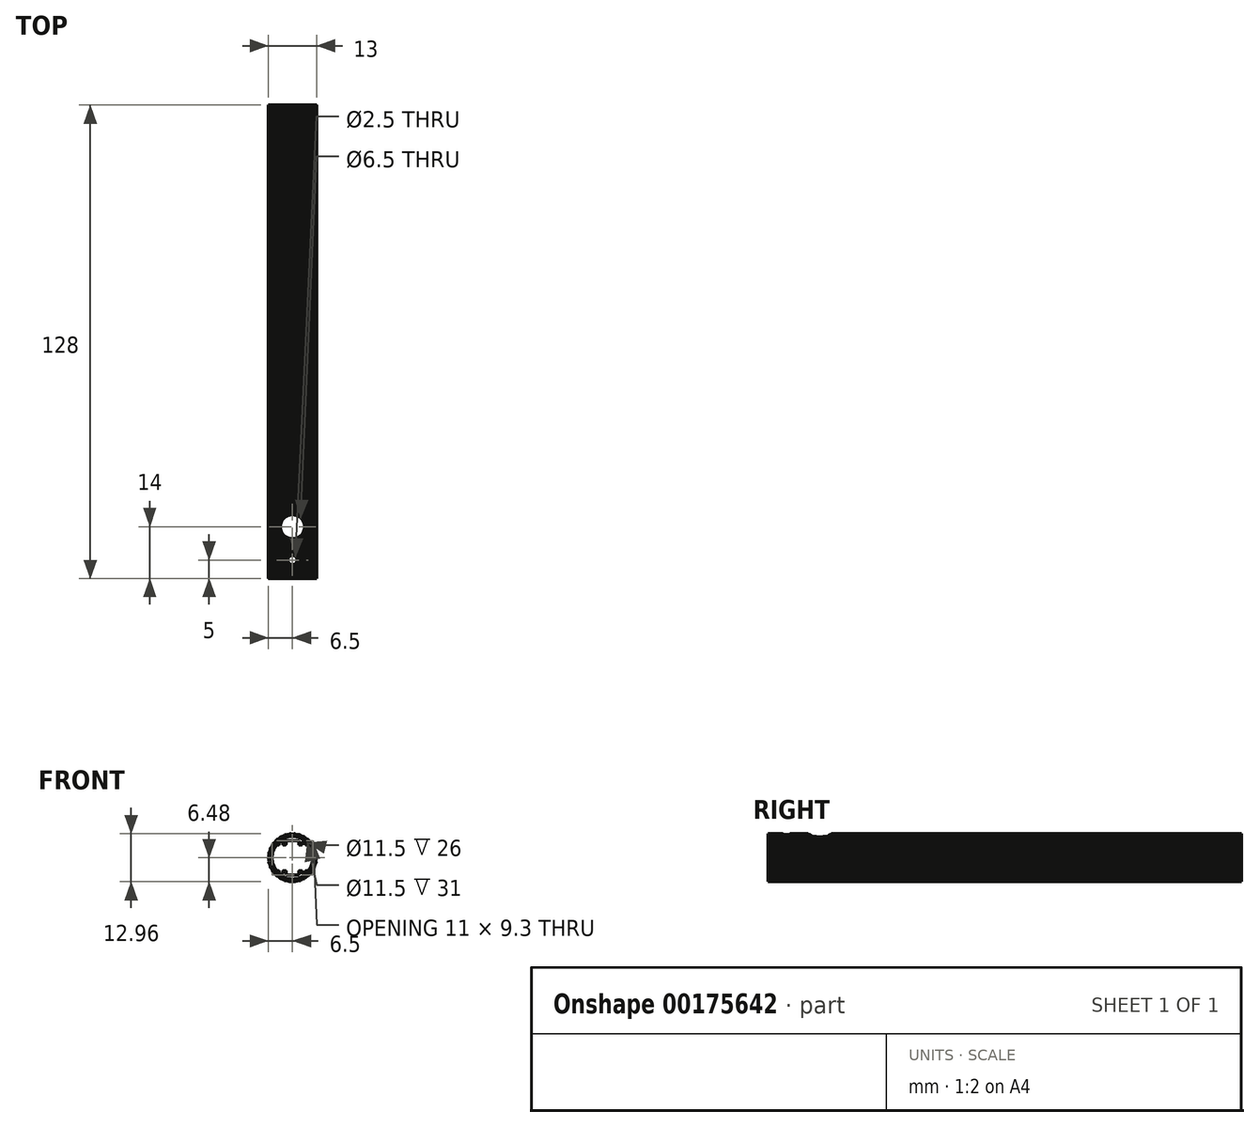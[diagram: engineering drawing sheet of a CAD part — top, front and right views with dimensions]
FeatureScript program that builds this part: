
annotation { "Feature Type Name" : "Feature", "Feature Type Description" : "" }
export const myFeature = defineFeature(function(context is Context, id is Id, definition is map)
    precondition{}
    {
        {
            assignVariable(context, id + "F0", {"name" : "Main_Length", "anyValue" : 128});
        }
        {
            assignVariable(context, id + "F1", {"name" : "Bore_Depth_F", "anyValue" : 26});
        }
        {
            assignVariable(context, id + "F2", {"name" : "Bore_Depth_R", "anyValue" : 31});
        }
        {
            var Q0;
            Q0=qCreatedBy(makeId("Front.planeOp"),FACE);
            var sketch = newSketch(context, id + "F3", { "sketchPlane" : qUnion([Q0])});
            skLineSegment(sketch, "E0", {"start": v(-3.5, -2.5) * mm, "end": v(-3.5, -1.85) * mm});
            skLineSegment(sketch, "E1", {"start": v(6.33, 0.97) * mm, "end": v(6.44, 0.88) * mm});
            skArc(sketch, "E2", {"start": v(-3.6, -1.75) * mm, "mid": v(-3.53, -1.78) * mm, "end": v(-3.5, -1.85) * mm});
            skArc(sketch, "E3", {"start": v(4.25, 3.55) * mm, "mid": v(4.32, 3.52) * mm, "end": v(4.35, 3.45) * mm});
            skArc(sketch, "E4", {"start": v(-3.5, -4.24) * mm, "mid": v(0, -5.5) * mm, "end": v(3.5, -4.24) * mm});
            skLineSegment(sketch, "E5", {"start": v(1.03, 6.32) * mm, "end": v(1.16, 6.4) * mm});
            skLineSegment(sketch, "E6", {"start": v(-4.95, -4.05) * mm, "end": v(-4.96, -4.2) * mm});
            skArc(sketch, "E7", {"start": v(-5.73, -3.08) * mm, "mid": v(-5.63, -3.25) * mm, "end": v(-5.53, -3.42) * mm});
            skLineSegment(sketch, "E8", {"start": v(3.51, 5.35) * mm, "end": v(3.66, 5.37) * mm});
            skLineSegment(sketch, "E9", {"start": v(4.65, -1.65) * mm, "end": v(4.65, 0) * mm});
            skLineSegment(sketch, "E10", {"start": v(-1.63, -6.19) * mm, "end": v(-1.55, -6.31) * mm});
            skArc(sketch, "E11", {"start": v(6.12, -2.2) * mm, "mid": v(6.18, -2) * mm, "end": v(6.24, -1.82) * mm});
            skArc(sketch, "E12", {"start": v(-2.83, -5.85) * mm, "mid": v(-2.64, -5.94) * mm, "end": v(-2.46, -6.02) * mm});
            skArc(sketch, "E13", {"start": v(2.83, 5.85) * mm, "mid": v(2.64, 5.94) * mm, "end": v(2.46, 6.02) * mm});
            skLineSegment(sketch, "E14", {"start": v(4.55, 4.5) * mm, "end": v(4.7, 4.5) * mm});
            skArc(sketch, "E15", {"start": v(-4.35, 2.7) * mm, "mid": v(-4.32, 2.63) * mm, "end": v(-4.25, 2.6) * mm});
            skArc(sketch, "E16", {"start": v(3.98, 5.14) * mm, "mid": v(3.82, 5.26) * mm, "end": v(3.66, 5.37) * mm});
            skLineSegment(sketch, "E17", {"start": v(-6.33, 0.97) * mm, "end": v(-6.44, 0.88) * mm});
            skArc(sketch, "E18", {"start": v(1.16, -6.4) * mm, "mid": v(1.35, -6.36) * mm, "end": v(1.55, -6.31) * mm});
            skLineSegment(sketch, "E19", {"start": v(-4, 5) * mm, "end": v(-3.98, 5.14) * mm});
            skArc(sketch, "E20", {"start": v(-1.55, -6.31) * mm, "mid": v(-1.35, -6.36) * mm, "end": v(-1.16, -6.4) * mm});
            skLineSegment(sketch, "E21", {"start": v(5.38, 3.46) * mm, "end": v(5.53, 3.42) * mm});
            skLineSegment(sketch, "E22", {"start": v(1.63, 6.19) * mm, "end": v(1.55, 6.31) * mm});
            skArc(sketch, "E23", {"start": v(3.5, -2.5) * mm, "mid": v(3.53, -2.57) * mm, "end": v(3.6, -2.6) * mm});
            skLineSegment(sketch, "E24", {"start": v(4, -5) * mm, "end": v(3.98, -5.14) * mm});
            skArc(sketch, "E25", {"start": v(3.6, 1.75) * mm, "mid": v(3.53, 1.78) * mm, "end": v(3.5, 1.85) * mm});
            skArc(sketch, "E26", {"start": v(2.88, -5.72) * mm, "mid": v(3.2, -5.54) * mm, "end": v(3.51, -5.35) * mm});
            skArc(sketch, "E27", {"start": v(-3.6, 3.55) * mm, "mid": v(-3.53, 3.58) * mm, "end": v(-3.5, 3.65) * mm});
            skArc(sketch, "E28", {"start": v(-5.53, 3.42) * mm, "mid": v(-5.63, 3.25) * mm, "end": v(-5.73, 3.08) * mm});
            skLineSegment(sketch, "E29", {"start": v(5.38, -3.46) * mm, "end": v(5.53, -3.42) * mm});
            skArc(sketch, "E30", {"start": v(5.73, 3.08) * mm, "mid": v(5.63, 3.25) * mm, "end": v(5.53, 3.42) * mm});
            skLineSegment(sketch, "E31", {"start": v(-4.25, 2.6) * mm, "end": v(-3.6, 2.6) * mm});
            skLineSegment(sketch, "E32", {"start": v(-3.5, 2.5) * mm, "end": v(-3.5, 1.85) * mm});
            skArc(sketch, "E33", {"start": v(6.24, 1.82) * mm, "mid": v(6.18, 2) * mm, "end": v(6.12, 2.2) * mm});
            skLineSegment(sketch, "E34", {"start": v(4.25, 2.6) * mm, "end": v(3.6, 2.6) * mm});
            skLineSegment(sketch, "E35", {"start": v(2.88, -5.72) * mm, "end": v(2.83, -5.85) * mm});
            skLineSegment(sketch, "E36", {"start": v(3.5, 4.24) * mm, "end": v(3.5, 3.65) * mm});
            skArc(sketch, "E37", {"start": v(5.99, 2.26) * mm, "mid": v(5.85, 2.6) * mm, "end": v(5.69, 2.93) * mm});
            skArc(sketch, "E38", {"start": v(0.3, -6.4) * mm, "mid": v(0.67, -6.36) * mm, "end": v(1.03, -6.32) * mm});
            skArc(sketch, "E39", {"start": v(6.48, 0.48) * mm, "mid": v(6.46, 0.68) * mm, "end": v(6.44, 0.88) * mm});
            skArc(sketch, "E40", {"start": v(-2.88, 5.72) * mm, "mid": v(-3.2, 5.54) * mm, "end": v(-3.51, 5.35) * mm});
            skLineSegment(sketch, "E41", {"start": v(-0.3, 6.4) * mm, "end": v(-0.2, 6.5) * mm});
            skLineSegment(sketch, "E42", {"start": v(5.69, 2.93) * mm, "end": v(5.73, 3.08) * mm});
            skLineSegment(sketch, "E43", {"start": v(1.63, -6.19) * mm, "end": v(1.55, -6.31) * mm});
            skArc(sketch, "E44", {"start": v(-0.3, 6.4) * mm, "mid": v(-0.67, 6.36) * mm, "end": v(-1.03, 6.32) * mm});
            skLineSegment(sketch, "E45", {"start": v(-3.51, 5.35) * mm, "end": v(-3.66, 5.37) * mm});
            skLineSegment(sketch, "E46", {"start": v(-1.63, 6.19) * mm, "end": v(-1.55, 6.31) * mm});
            skLineSegment(sketch, "E47", {"start": v(4.55, -4.5) * mm, "end": v(4.7, -4.5) * mm});
            skArc(sketch, "E48", {"start": v(6.44, -0.88) * mm, "mid": v(6.46, -0.68) * mm, "end": v(6.48, -0.48) * mm});
            skArc(sketch, "E49", {"start": v(-2.46, 6.02) * mm, "mid": v(-2.64, 5.94) * mm, "end": v(-2.83, 5.85) * mm});
            skArc(sketch, "E50", {"start": v(6.33, 0.97) * mm, "mid": v(6.26, 1.33) * mm, "end": v(6.17, 1.69) * mm});
            skArc(sketch, "E51", {"start": v(3.6, 3.55) * mm, "mid": v(3.53, 3.58) * mm, "end": v(3.5, 3.65) * mm});
            skLineSegment(sketch, "E52", {"start": v(3.5, 2.5) * mm, "end": v(3.5, 1.85) * mm});
            skArc(sketch, "E53", {"start": v(-0.2, -6.5) * mm, "mid": v(0, -6.5) * mm, "end": v(0.2, -6.5) * mm});
            skArc(sketch, "E54", {"start": v(4.96, 4.2) * mm, "mid": v(4.83, 4.35) * mm, "end": v(4.7, 4.5) * mm});
            skLineSegment(sketch, "E55", {"start": v(2.32, 5.96) * mm, "end": v(2.46, 6.02) * mm});
            skArc(sketch, "E56", {"start": v(4.35, 2.7) * mm, "mid": v(4.32, 2.63) * mm, "end": v(4.25, 2.6) * mm});
            skLineSegment(sketch, "E57", {"start": v(-4.65, -1.65) * mm, "end": v(-4.65, 0) * mm});
            skArc(sketch, "E58", {"start": v(-1.63, 6.19) * mm, "mid": v(-1.98, 6.09) * mm, "end": v(-2.32, 5.96) * mm});
            skLineSegment(sketch, "E59", {"start": v(-1.03, 6.32) * mm, "end": v(-1.16, 6.4) * mm});
            skLineSegment(sketch, "E60", {"start": v(0.3, -6.4) * mm, "end": v(0.2, -6.5) * mm});
            skArc(sketch, "E61", {"start": v(-4.7, 4.5) * mm, "mid": v(-4.83, 4.35) * mm, "end": v(-4.96, 4.2) * mm});
            skArc(sketch, "E62", {"start": v(-5.69, 2.93) * mm, "mid": v(-5.85, 2.6) * mm, "end": v(-5.99, 2.26) * mm});
            skArc(sketch, "E63", {"start": v(4.25, -3.55) * mm, "mid": v(4.32, -3.52) * mm, "end": v(4.35, -3.45) * mm});
            skLineSegment(sketch, "E64", {"start": v(-4.35, 3.45) * mm, "end": v(-4.35, 2.7) * mm});
            skLineSegment(sketch, "E65", {"start": v(-4.65, 1.65) * mm, "end": v(-4.65, 0) * mm});
            skArc(sketch, "E66", {"start": v(5.69, -2.93) * mm, "mid": v(5.85, -2.6) * mm, "end": v(5.99, -2.26) * mm});
            skArc(sketch, "E67", {"start": v(-4.55, 1.75) * mm, "mid": v(-4.62, 1.72) * mm, "end": v(-4.65, 1.65) * mm});
            skLineSegment(sketch, "E68", {"start": v(-3.5, 4.24) * mm, "end": v(-3.5, 3.65) * mm});
            skLineSegment(sketch, "E69", {"start": v(-3.6, 3.55) * mm, "end": v(-4.25, 3.55) * mm});
            skLineSegment(sketch, "E70", {"start": v(-3.6, 1.75) * mm, "end": v(-4.55, 1.75) * mm});
            skArc(sketch, "E71", {"start": v(-3.5, 2.5) * mm, "mid": v(-3.53, 2.57) * mm, "end": v(-3.6, 2.6) * mm});
            skArc(sketch, "E72", {"start": v(-3.6, 1.75) * mm, "mid": v(-3.53, 1.78) * mm, "end": v(-3.5, 1.85) * mm});
            skArc(sketch, "E73", {"start": v(-4.25, 3.55) * mm, "mid": v(-4.32, 3.52) * mm, "end": v(-4.35, 3.45) * mm});
            skArc(sketch, "E74", {"start": v(4.55, 1.75) * mm, "mid": v(4.62, 1.72) * mm, "end": v(4.65, 1.65) * mm});
            skLineSegment(sketch, "E75", {"start": v(3.6, 1.75) * mm, "end": v(4.55, 1.75) * mm});
            skArc(sketch, "E76", {"start": v(3.5, 2.5) * mm, "mid": v(3.53, 2.57) * mm, "end": v(3.6, 2.6) * mm});
            skArc(sketch, "E77", {"start": v(0.2, 6.5) * mm, "mid": v(0, 6.5) * mm, "end": v(-0.2, 6.5) * mm});
            skLineSegment(sketch, "E78", {"start": v(3.6, 3.55) * mm, "end": v(4.25, 3.55) * mm});
            skLineSegment(sketch, "E79", {"start": v(4.65, 1.65) * mm, "end": v(4.65, 0) * mm});
            skLineSegment(sketch, "E80", {"start": v(4.35, 3.45) * mm, "end": v(4.35, 2.7) * mm});
            skArc(sketch, "E81", {"start": v(-3.6, -3.55) * mm, "mid": v(-3.53, -3.58) * mm, "end": v(-3.5, -3.65) * mm});
            skLineSegment(sketch, "E82", {"start": v(-4.25, -2.6) * mm, "end": v(-3.6, -2.6) * mm});
            skLineSegment(sketch, "E83", {"start": v(-3.6, -1.75) * mm, "end": v(-4.55, -1.75) * mm});
            skArc(sketch, "E84", {"start": v(-3.5, -2.5) * mm, "mid": v(-3.53, -2.57) * mm, "end": v(-3.6, -2.6) * mm});
            skArc(sketch, "E85", {"start": v(-4.55, -1.75) * mm, "mid": v(-4.62, -1.72) * mm, "end": v(-4.65, -1.65) * mm});
            skArc(sketch, "E86", {"start": v(-4.35, -2.7) * mm, "mid": v(-4.32, -2.63) * mm, "end": v(-4.25, -2.6) * mm});
            skArc(sketch, "E87", {"start": v(-4.25, -3.55) * mm, "mid": v(-4.32, -3.52) * mm, "end": v(-4.35, -3.45) * mm});
            skArc(sketch, "E88", {"start": v(3.6, -1.75) * mm, "mid": v(3.53, -1.78) * mm, "end": v(3.5, -1.85) * mm});
            skLineSegment(sketch, "E89", {"start": v(-2.32, 5.96) * mm, "end": v(-2.46, 6.02) * mm});
            skArc(sketch, "E90", {"start": v(4.55, -1.75) * mm, "mid": v(4.62, -1.72) * mm, "end": v(4.65, -1.65) * mm});
            skLineSegment(sketch, "E91", {"start": v(3.6, -1.75) * mm, "end": v(4.55, -1.75) * mm});
            skArc(sketch, "E92", {"start": v(4.35, -2.7) * mm, "mid": v(4.32, -2.63) * mm, "end": v(4.25, -2.6) * mm});
            skLineSegment(sketch, "E93", {"start": v(4.25, -2.6) * mm, "end": v(3.6, -2.6) * mm});
            skArc(sketch, "E94", {"start": v(3.6, -3.55) * mm, "mid": v(3.53, -3.58) * mm, "end": v(3.5, -3.65) * mm});
            skLineSegment(sketch, "E95", {"start": v(-3.5, -4.24) * mm, "end": v(-3.5, -3.65) * mm});
            skLineSegment(sketch, "E96", {"start": v(3.5, -2.5) * mm, "end": v(3.5, -1.85) * mm});
            skLineSegment(sketch, "E97", {"start": v(4.35, -3.45) * mm, "end": v(4.35, -2.7) * mm});
            skLineSegment(sketch, "E98", {"start": v(-3.6, -3.55) * mm, "end": v(-4.25, -3.55) * mm});
            skArc(sketch, "E99", {"start": v(-6.12, 2.2) * mm, "mid": v(-6.18, 2) * mm, "end": v(-6.24, 1.82) * mm});
            skLineSegment(sketch, "E100", {"start": v(-4.35, -3.45) * mm, "end": v(-4.35, -2.7) * mm});
            skLineSegment(sketch, "E101", {"start": v(3.6, -3.55) * mm, "end": v(4.25, -3.55) * mm});
            skLineSegment(sketch, "E102", {"start": v(-5.38, 3.46) * mm, "end": v(-5.53, 3.42) * mm});
            skLineSegment(sketch, "E103", {"start": v(3.5, -4.24) * mm, "end": v(3.5, -3.65) * mm});
            skArc(sketch, "E104", {"start": v(3.5, 4.24) * mm, "mid": v(0, 5.5) * mm, "end": v(-3.5, 4.24) * mm});
            skLineSegment(sketch, "E105", {"start": v(-0.3, -6.4) * mm, "end": v(-0.2, -6.5) * mm});
            skArc(sketch, "E106", {"start": v(1.63, -6.19) * mm, "mid": v(1.98, -6.09) * mm, "end": v(2.32, -5.96) * mm});
            skLineSegment(sketch, "E107", {"start": v(1.03, -6.32) * mm, "end": v(1.16, -6.4) * mm});
            skArc(sketch, "E108", {"start": v(2.46, -6.02) * mm, "mid": v(2.64, -5.94) * mm, "end": v(2.83, -5.85) * mm});
            skArc(sketch, "E109", {"start": v(-6.24, -1.82) * mm, "mid": v(-6.18, -2) * mm, "end": v(-6.12, -2.2) * mm});
            skLineSegment(sketch, "E110", {"start": v(2.32, -5.96) * mm, "end": v(2.46, -6.02) * mm});
            skArc(sketch, "E111", {"start": v(4, -5) * mm, "mid": v(4.28, -4.76) * mm, "end": v(4.55, -4.5) * mm});
            skArc(sketch, "E112", {"start": v(3.66, -5.37) * mm, "mid": v(3.82, -5.26) * mm, "end": v(3.98, -5.14) * mm});
            skLineSegment(sketch, "E113", {"start": v(3.51, -5.35) * mm, "end": v(3.66, -5.37) * mm});
            skLineSegment(sketch, "E114", {"start": v(-3.51, -5.35) * mm, "end": v(-3.66, -5.37) * mm});
            skLineSegment(sketch, "E115", {"start": v(4.95, -4.05) * mm, "end": v(4.96, -4.2) * mm});
            skLineSegment(sketch, "E116", {"start": v(-4.55, -4.5) * mm, "end": v(-4.7, -4.5) * mm});
            skArc(sketch, "E117", {"start": v(5.53, -3.42) * mm, "mid": v(5.63, -3.25) * mm, "end": v(5.73, -3.08) * mm});
            skArc(sketch, "E118", {"start": v(4.7, -4.5) * mm, "mid": v(4.83, -4.35) * mm, "end": v(4.96, -4.2) * mm});
            skArc(sketch, "E119", {"start": v(-3.98, -5.14) * mm, "mid": v(-3.82, -5.26) * mm, "end": v(-3.66, -5.37) * mm});
            skArc(sketch, "E120", {"start": v(6.17, -1.69) * mm, "mid": v(6.26, -1.33) * mm, "end": v(6.33, -0.97) * mm});
            skLineSegment(sketch, "E121", {"start": v(6.17, -1.69) * mm, "end": v(6.24, -1.82) * mm});
            skLineSegment(sketch, "E122", {"start": v(5.99, -2.26) * mm, "end": v(6.12, -2.2) * mm});
            skArc(sketch, "E123", {"start": v(6.39, -0.37) * mm, "mid": v(6.4, 0) * mm, "end": v(6.39, 0.37) * mm});
            skLineSegment(sketch, "E124", {"start": v(6.39, -0.37) * mm, "end": v(6.48, -0.48) * mm});
            skLineSegment(sketch, "E125", {"start": v(-1.03, -6.32) * mm, "end": v(-1.16, -6.4) * mm});
            skLineSegment(sketch, "E126", {"start": v(6.33, -0.97) * mm, "end": v(6.44, -0.88) * mm});
            skLineSegment(sketch, "E127", {"start": v(5.99, 2.26) * mm, "end": v(6.12, 2.2) * mm});
            skLineSegment(sketch, "E128", {"start": v(6.17, 1.69) * mm, "end": v(6.24, 1.82) * mm});
            skArc(sketch, "E129", {"start": v(5.38, 3.46) * mm, "mid": v(5.18, 3.76) * mm, "end": v(4.95, 4.05) * mm});
            skArc(sketch, "E130", {"start": v(4.55, 4.5) * mm, "mid": v(4.28, 4.76) * mm, "end": v(4, 5) * mm});
            skLineSegment(sketch, "E131", {"start": v(4.95, 4.05) * mm, "end": v(4.96, 4.2) * mm});
            skArc(sketch, "E132", {"start": v(3.51, 5.35) * mm, "mid": v(3.2, 5.54) * mm, "end": v(2.88, 5.72) * mm});
            skLineSegment(sketch, "E133", {"start": v(4, 5) * mm, "end": v(3.98, 5.14) * mm});
            skArc(sketch, "E134", {"start": v(2.32, 5.96) * mm, "mid": v(1.98, 6.09) * mm, "end": v(1.63, 6.19) * mm});
            skLineSegment(sketch, "E135", {"start": v(2.88, 5.72) * mm, "end": v(2.83, 5.85) * mm});
            skArc(sketch, "E136", {"start": v(1.03, 6.32) * mm, "mid": v(0.67, 6.36) * mm, "end": v(0.3, 6.4) * mm});
            skArc(sketch, "E137", {"start": v(1.55, 6.31) * mm, "mid": v(1.35, 6.36) * mm, "end": v(1.16, 6.4) * mm});
            skLineSegment(sketch, "E138", {"start": v(0.3, 6.4) * mm, "end": v(0.2, 6.5) * mm});
            skArc(sketch, "E139", {"start": v(-1.16, 6.4) * mm, "mid": v(-1.35, 6.36) * mm, "end": v(-1.55, 6.31) * mm});
            skLineSegment(sketch, "E140", {"start": v(-2.88, 5.72) * mm, "end": v(-2.83, 5.85) * mm});
            skArc(sketch, "E141", {"start": v(-4, 5) * mm, "mid": v(-4.28, 4.76) * mm, "end": v(-4.55, 4.5) * mm});
            skArc(sketch, "E142", {"start": v(-3.66, 5.37) * mm, "mid": v(-3.82, 5.26) * mm, "end": v(-3.98, 5.14) * mm});
            skLineSegment(sketch, "E143", {"start": v(-6.33, -0.97) * mm, "end": v(-6.44, -0.88) * mm});
            skLineSegment(sketch, "E144", {"start": v(-4.95, 4.05) * mm, "end": v(-4.96, 4.2) * mm});
            skLineSegment(sketch, "E145", {"start": v(-4.55, 4.5) * mm, "end": v(-4.7, 4.5) * mm});
            skArc(sketch, "E146", {"start": v(-6.17, 1.69) * mm, "mid": v(-6.26, 1.33) * mm, "end": v(-6.33, 0.97) * mm});
            skLineSegment(sketch, "E147", {"start": v(-6.17, 1.69) * mm, "end": v(-6.24, 1.82) * mm});
            skLineSegment(sketch, "E148", {"start": v(-5.99, 2.26) * mm, "end": v(-6.12, 2.2) * mm});
            skArc(sketch, "E149", {"start": v(-6.39, 0.37) * mm, "mid": v(-6.4, 0) * mm, "end": v(-6.39, -0.37) * mm});
            skArc(sketch, "E150", {"start": v(-6.44, 0.88) * mm, "mid": v(-6.46, 0.68) * mm, "end": v(-6.48, 0.48) * mm});
            skLineSegment(sketch, "E151", {"start": v(-6.39, 0.37) * mm, "end": v(-6.48, 0.48) * mm});
            skLineSegment(sketch, "E152", {"start": v(5.69, -2.93) * mm, "end": v(5.73, -3.08) * mm});
            skArc(sketch, "E153", {"start": v(-6.33, -0.97) * mm, "mid": v(-6.26, -1.33) * mm, "end": v(-6.17, -1.69) * mm});
            skArc(sketch, "E154", {"start": v(-6.48, -0.48) * mm, "mid": v(-6.46, -0.68) * mm, "end": v(-6.44, -0.88) * mm});
            skLineSegment(sketch, "E155", {"start": v(-6.39, -0.37) * mm, "end": v(-6.48, -0.48) * mm});
            skArc(sketch, "E156", {"start": v(-5.99, -2.26) * mm, "mid": v(-5.85, -2.6) * mm, "end": v(-5.69, -2.93) * mm});
            skLineSegment(sketch, "E157", {"start": v(-5.99, -2.26) * mm, "end": v(-6.12, -2.2) * mm});
            skLineSegment(sketch, "E158", {"start": v(-6.17, -1.69) * mm, "end": v(-6.24, -1.82) * mm});
            skArc(sketch, "E159", {"start": v(-5.38, -3.46) * mm, "mid": v(-5.18, -3.76) * mm, "end": v(-4.95, -4.05) * mm});
            skLineSegment(sketch, "E160", {"start": v(-5.38, -3.46) * mm, "end": v(-5.53, -3.42) * mm});
            skLineSegment(sketch, "E161", {"start": v(-5.69, -2.93) * mm, "end": v(-5.73, -3.08) * mm});
            skArc(sketch, "E162", {"start": v(-4.55, -4.5) * mm, "mid": v(-4.28, -4.76) * mm, "end": v(-4, -5) * mm});
            skLineSegment(sketch, "E163", {"start": v(6.39, 0.37) * mm, "end": v(6.48, 0.48) * mm});
            skArc(sketch, "E164", {"start": v(-4.96, -4.2) * mm, "mid": v(-4.83, -4.35) * mm, "end": v(-4.7, -4.5) * mm});
            skArc(sketch, "E165", {"start": v(4.95, -4.05) * mm, "mid": v(5.18, -3.76) * mm, "end": v(5.38, -3.46) * mm});
            skLineSegment(sketch, "E166", {"start": v(-4, -5) * mm, "end": v(-3.98, -5.14) * mm});
            skArc(sketch, "E167", {"start": v(-2.32, -5.96) * mm, "mid": v(-1.98, -6.09) * mm, "end": v(-1.63, -6.19) * mm});
            skLineSegment(sketch, "E168", {"start": v(-2.32, -5.96) * mm, "end": v(-2.46, -6.02) * mm});
            skLineSegment(sketch, "E169", {"start": v(-2.88, -5.72) * mm, "end": v(-2.83, -5.85) * mm});
            skArc(sketch, "E170", {"start": v(-1.03, -6.32) * mm, "mid": v(-0.67, -6.36) * mm, "end": v(-0.3, -6.4) * mm});
            skArc(sketch, "E171", {"start": v(-4.95, 4.05) * mm, "mid": v(-5.18, 3.76) * mm, "end": v(-5.38, 3.46) * mm});
            skLineSegment(sketch, "E172", {"start": v(-5.69, 2.93) * mm, "end": v(-5.73, 3.08) * mm});
            skArc(sketch, "E173", {"start": v(-3.51, -5.35) * mm, "mid": v(-3.2, -5.54) * mm, "end": v(-2.88, -5.72) * mm});
            skSolve(sketch);
        }
        {
            var Q0;
            Q0=makeQuery(id+"F3.imprint","IMPRINT",FACE,{"disambiguationData":[TD([[makeQuery(id+"F3.imprint","IMPRINT",EDGE,{"derivedFrom":sQuery(id+"F3.wireOp",EDGE,"E0")}),1.0]])]});
            extrude(context, id + "F4", {"entities" : qUnion([Q0]), "depth" : (getVariable(context, 'Main_Length') - getVariable(context, 'Bore_Depth_F') - getVariable(context, 'Bore_Depth_R')) * mm});
        }
        {
            var Q0;
            Q0=makeQuery(id+"F4.opExtrude","CAP_FACE",FACE,{"disambiguationData":[OSD([sQuery(id+"F3.wireOp",EDGE,"E0"),sQuery(id+"F3.wireOp",EDGE,"E1"),sQuery(id+"F3.wireOp",EDGE,"E2"),sQuery(id+"F3.wireOp",EDGE,"E3"),sQuery(id+"F3.wireOp",EDGE,"E4"),sQuery(id+"F3.wireOp",EDGE,"E5"),sQuery(id+"F3.wireOp",EDGE,"E6"),sQuery(id+"F3.wireOp",EDGE,"E7"),sQuery(id+"F3.wireOp",EDGE,"E8"),sQuery(id+"F3.wireOp",EDGE,"E9"),sQuery(id+"F3.wireOp",EDGE,"E10"),sQuery(id+"F3.wireOp",EDGE,"E11"),sQuery(id+"F3.wireOp",EDGE,"E12"),sQuery(id+"F3.wireOp",EDGE,"E13"),sQuery(id+"F3.wireOp",EDGE,"E14"),sQuery(id+"F3.wireOp",EDGE,"E15"),sQuery(id+"F3.wireOp",EDGE,"E16"),sQuery(id+"F3.wireOp",EDGE,"E17"),sQuery(id+"F3.wireOp",EDGE,"E18"),sQuery(id+"F3.wireOp",EDGE,"E19"),sQuery(id+"F3.wireOp",EDGE,"E20"),sQuery(id+"F3.wireOp",EDGE,"E21"),sQuery(id+"F3.wireOp",EDGE,"E22"),sQuery(id+"F3.wireOp",EDGE,"E23"),sQuery(id+"F3.wireOp",EDGE,"E24"),sQuery(id+"F3.wireOp",EDGE,"E25"),sQuery(id+"F3.wireOp",EDGE,"E26"),sQuery(id+"F3.wireOp",EDGE,"E27"),sQuery(id+"F3.wireOp",EDGE,"E28"),sQuery(id+"F3.wireOp",EDGE,"E29"),sQuery(id+"F3.wireOp",EDGE,"E30"),sQuery(id+"F3.wireOp",EDGE,"E31"),sQuery(id+"F3.wireOp",EDGE,"E32"),sQuery(id+"F3.wireOp",EDGE,"E33"),sQuery(id+"F3.wireOp",EDGE,"E34"),sQuery(id+"F3.wireOp",EDGE,"E35"),sQuery(id+"F3.wireOp",EDGE,"E36"),sQuery(id+"F3.wireOp",EDGE,"E37"),sQuery(id+"F3.wireOp",EDGE,"E38"),sQuery(id+"F3.wireOp",EDGE,"E39"),sQuery(id+"F3.wireOp",EDGE,"E40"),sQuery(id+"F3.wireOp",EDGE,"E41"),sQuery(id+"F3.wireOp",EDGE,"E42"),sQuery(id+"F3.wireOp",EDGE,"E43"),sQuery(id+"F3.wireOp",EDGE,"E44"),sQuery(id+"F3.wireOp",EDGE,"E45"),sQuery(id+"F3.wireOp",EDGE,"E46"),sQuery(id+"F3.wireOp",EDGE,"E47"),sQuery(id+"F3.wireOp",EDGE,"E48"),sQuery(id+"F3.wireOp",EDGE,"E49"),sQuery(id+"F3.wireOp",EDGE,"E50"),sQuery(id+"F3.wireOp",EDGE,"E51"),sQuery(id+"F3.wireOp",EDGE,"E52"),sQuery(id+"F3.wireOp",EDGE,"E53"),sQuery(id+"F3.wireOp",EDGE,"E54"),sQuery(id+"F3.wireOp",EDGE,"E55"),sQuery(id+"F3.wireOp",EDGE,"E56"),sQuery(id+"F3.wireOp",EDGE,"E57"),sQuery(id+"F3.wireOp",EDGE,"E58"),sQuery(id+"F3.wireOp",EDGE,"E59"),sQuery(id+"F3.wireOp",EDGE,"E60"),sQuery(id+"F3.wireOp",EDGE,"E61"),sQuery(id+"F3.wireOp",EDGE,"E62"),sQuery(id+"F3.wireOp",EDGE,"E63"),sQuery(id+"F3.wireOp",EDGE,"E64"),sQuery(id+"F3.wireOp",EDGE,"E65"),sQuery(id+"F3.wireOp",EDGE,"E66"),sQuery(id+"F3.wireOp",EDGE,"E67"),sQuery(id+"F3.wireOp",EDGE,"E68"),sQuery(id+"F3.wireOp",EDGE,"E69"),sQuery(id+"F3.wireOp",EDGE,"E70"),sQuery(id+"F3.wireOp",EDGE,"E71"),sQuery(id+"F3.wireOp",EDGE,"E72"),sQuery(id+"F3.wireOp",EDGE,"E73"),sQuery(id+"F3.wireOp",EDGE,"E74"),sQuery(id+"F3.wireOp",EDGE,"E75"),sQuery(id+"F3.wireOp",EDGE,"E76"),sQuery(id+"F3.wireOp",EDGE,"E77"),sQuery(id+"F3.wireOp",EDGE,"E78"),sQuery(id+"F3.wireOp",EDGE,"E79"),sQuery(id+"F3.wireOp",EDGE,"E80"),sQuery(id+"F3.wireOp",EDGE,"E81"),sQuery(id+"F3.wireOp",EDGE,"E82"),sQuery(id+"F3.wireOp",EDGE,"E83"),sQuery(id+"F3.wireOp",EDGE,"E84"),sQuery(id+"F3.wireOp",EDGE,"E85"),sQuery(id+"F3.wireOp",EDGE,"E86"),sQuery(id+"F3.wireOp",EDGE,"E87"),sQuery(id+"F3.wireOp",EDGE,"E88"),sQuery(id+"F3.wireOp",EDGE,"E89"),sQuery(id+"F3.wireOp",EDGE,"E90"),sQuery(id+"F3.wireOp",EDGE,"E91"),sQuery(id+"F3.wireOp",EDGE,"E92"),sQuery(id+"F3.wireOp",EDGE,"E93"),sQuery(id+"F3.wireOp",EDGE,"E94"),sQuery(id+"F3.wireOp",EDGE,"E95"),sQuery(id+"F3.wireOp",EDGE,"E96"),sQuery(id+"F3.wireOp",EDGE,"E97"),sQuery(id+"F3.wireOp",EDGE,"E98"),sQuery(id+"F3.wireOp",EDGE,"E99"),sQuery(id+"F3.wireOp",EDGE,"E100"),sQuery(id+"F3.wireOp",EDGE,"E101"),sQuery(id+"F3.wireOp",EDGE,"E102"),sQuery(id+"F3.wireOp",EDGE,"E103"),sQuery(id+"F3.wireOp",EDGE,"E104"),sQuery(id+"F3.wireOp",EDGE,"E105"),sQuery(id+"F3.wireOp",EDGE,"E106"),sQuery(id+"F3.wireOp",EDGE,"E107"),sQuery(id+"F3.wireOp",EDGE,"E108"),sQuery(id+"F3.wireOp",EDGE,"E109"),sQuery(id+"F3.wireOp",EDGE,"E110"),sQuery(id+"F3.wireOp",EDGE,"E111"),sQuery(id+"F3.wireOp",EDGE,"E112"),sQuery(id+"F3.wireOp",EDGE,"E113"),sQuery(id+"F3.wireOp",EDGE,"E114"),sQuery(id+"F3.wireOp",EDGE,"E115"),sQuery(id+"F3.wireOp",EDGE,"E116"),sQuery(id+"F3.wireOp",EDGE,"E117"),sQuery(id+"F3.wireOp",EDGE,"E118"),sQuery(id+"F3.wireOp",EDGE,"E119"),sQuery(id+"F3.wireOp",EDGE,"E120"),sQuery(id+"F3.wireOp",EDGE,"E121"),sQuery(id+"F3.wireOp",EDGE,"E122"),sQuery(id+"F3.wireOp",EDGE,"E123"),sQuery(id+"F3.wireOp",EDGE,"E124"),sQuery(id+"F3.wireOp",EDGE,"E125"),sQuery(id+"F3.wireOp",EDGE,"E126"),sQuery(id+"F3.wireOp",EDGE,"E127"),sQuery(id+"F3.wireOp",EDGE,"E128"),sQuery(id+"F3.wireOp",EDGE,"E129"),sQuery(id+"F3.wireOp",EDGE,"E130"),sQuery(id+"F3.wireOp",EDGE,"E131"),sQuery(id+"F3.wireOp",EDGE,"E132"),sQuery(id+"F3.wireOp",EDGE,"E133"),sQuery(id+"F3.wireOp",EDGE,"E134"),sQuery(id+"F3.wireOp",EDGE,"E135"),sQuery(id+"F3.wireOp",EDGE,"E136"),sQuery(id+"F3.wireOp",EDGE,"E137"),sQuery(id+"F3.wireOp",EDGE,"E138"),sQuery(id+"F3.wireOp",EDGE,"E139"),sQuery(id+"F3.wireOp",EDGE,"E140"),sQuery(id+"F3.wireOp",EDGE,"E141"),sQuery(id+"F3.wireOp",EDGE,"E142"),sQuery(id+"F3.wireOp",EDGE,"E143"),sQuery(id+"F3.wireOp",EDGE,"E144"),sQuery(id+"F3.wireOp",EDGE,"E145"),sQuery(id+"F3.wireOp",EDGE,"E146"),sQuery(id+"F3.wireOp",EDGE,"E147"),sQuery(id+"F3.wireOp",EDGE,"E148"),sQuery(id+"F3.wireOp",EDGE,"E149"),sQuery(id+"F3.wireOp",EDGE,"E150"),sQuery(id+"F3.wireOp",EDGE,"E151"),sQuery(id+"F3.wireOp",EDGE,"E152"),sQuery(id+"F3.wireOp",EDGE,"E153"),sQuery(id+"F3.wireOp",EDGE,"E154"),sQuery(id+"F3.wireOp",EDGE,"E155"),sQuery(id+"F3.wireOp",EDGE,"E156"),sQuery(id+"F3.wireOp",EDGE,"E157"),sQuery(id+"F3.wireOp",EDGE,"E158"),sQuery(id+"F3.wireOp",EDGE,"E159"),sQuery(id+"F3.wireOp",EDGE,"E160"),sQuery(id+"F3.wireOp",EDGE,"E161"),sQuery(id+"F3.wireOp",EDGE,"E162"),sQuery(id+"F3.wireOp",EDGE,"E163"),sQuery(id+"F3.wireOp",EDGE,"E164"),sQuery(id+"F3.wireOp",EDGE,"E165"),sQuery(id+"F3.wireOp",EDGE,"E166"),sQuery(id+"F3.wireOp",EDGE,"E167"),sQuery(id+"F3.wireOp",EDGE,"E168"),sQuery(id+"F3.wireOp",EDGE,"E169"),sQuery(id+"F3.wireOp",EDGE,"E170"),sQuery(id+"F3.wireOp",EDGE,"E171"),sQuery(id+"F3.wireOp",EDGE,"E172"),sQuery(id+"F3.wireOp",EDGE,"E173")])],"isStart":false});
            var sketch = newSketch(context, id + "F5", { "sketchPlane" : qUnion([Q0])});
            skCircle(sketch, "E174", {"center": v(0, 0) * mm, "radius": 5.75 * mm});
            skLineSegment(sketch, "E175.0.0", {"start": v(6.44, 0.88) * mm, "end": v(6.33, 0.97) * mm});
            skArc(sketch, "E175.0.1", {"start": v(6.33, 0.97) * mm, "mid": v(6.26, 1.33) * mm, "end": v(6.17, 1.69) * mm});
            skLineSegment(sketch, "E175.0.2", {"start": v(6.17, 1.69) * mm, "end": v(6.24, 1.82) * mm});
            skArc(sketch, "E175.0.3", {"start": v(6.24, 1.82) * mm, "mid": v(6.18, 2) * mm, "end": v(6.12, 2.2) * mm});
            skLineSegment(sketch, "E175.0.4", {"start": v(6.12, 2.2) * mm, "end": v(5.99, 2.26) * mm});
            skArc(sketch, "E175.0.5", {"start": v(5.99, 2.26) * mm, "mid": v(5.85, 2.6) * mm, "end": v(5.69, 2.93) * mm});
            skLineSegment(sketch, "E175.0.6", {"start": v(5.69, 2.93) * mm, "end": v(5.73, 3.08) * mm});
            skArc(sketch, "E175.0.7", {"start": v(5.73, 3.08) * mm, "mid": v(5.63, 3.25) * mm, "end": v(5.53, 3.42) * mm});
            skLineSegment(sketch, "E175.0.8", {"start": v(5.53, 3.42) * mm, "end": v(5.38, 3.46) * mm});
            skArc(sketch, "E175.0.9", {"start": v(5.38, 3.46) * mm, "mid": v(5.18, 3.76) * mm, "end": v(4.95, 4.05) * mm});
            skLineSegment(sketch, "E175.0.10", {"start": v(4.95, 4.05) * mm, "end": v(4.96, 4.2) * mm});
            skArc(sketch, "E175.0.11", {"start": v(4.96, 4.2) * mm, "mid": v(4.83, 4.35) * mm, "end": v(4.7, 4.5) * mm});
            skLineSegment(sketch, "E175.0.12", {"start": v(4.7, 4.5) * mm, "end": v(4.55, 4.5) * mm});
            skArc(sketch, "E175.0.13", {"start": v(4.55, 4.5) * mm, "mid": v(4.28, 4.76) * mm, "end": v(4, 5) * mm});
            skLineSegment(sketch, "E175.0.14", {"start": v(4, 5) * mm, "end": v(3.98, 5.14) * mm});
            skArc(sketch, "E175.0.15", {"start": v(3.98, 5.14) * mm, "mid": v(3.82, 5.26) * mm, "end": v(3.66, 5.37) * mm});
            skLineSegment(sketch, "E175.0.16", {"start": v(3.66, 5.37) * mm, "end": v(3.51, 5.35) * mm});
            skArc(sketch, "E175.0.17", {"start": v(3.51, 5.35) * mm, "mid": v(3.2, 5.54) * mm, "end": v(2.88, 5.72) * mm});
            skLineSegment(sketch, "E175.0.18", {"start": v(2.88, 5.72) * mm, "end": v(2.83, 5.85) * mm});
            skArc(sketch, "E175.0.19", {"start": v(2.83, 5.85) * mm, "mid": v(2.64, 5.94) * mm, "end": v(2.46, 6.02) * mm});
            skLineSegment(sketch, "E175.0.20", {"start": v(2.46, 6.02) * mm, "end": v(2.32, 5.96) * mm});
            skArc(sketch, "E175.0.21", {"start": v(2.32, 5.96) * mm, "mid": v(1.98, 6.09) * mm, "end": v(1.63, 6.19) * mm});
            skLineSegment(sketch, "E175.0.22", {"start": v(1.63, 6.19) * mm, "end": v(1.55, 6.31) * mm});
            skArc(sketch, "E175.0.23", {"start": v(1.55, 6.31) * mm, "mid": v(1.35, 6.36) * mm, "end": v(1.16, 6.4) * mm});
            skLineSegment(sketch, "E175.0.24", {"start": v(1.16, 6.4) * mm, "end": v(1.03, 6.32) * mm});
            skArc(sketch, "E175.0.25", {"start": v(1.03, 6.32) * mm, "mid": v(0.67, 6.36) * mm, "end": v(0.3, 6.4) * mm});
            skLineSegment(sketch, "E175.0.26", {"start": v(0.3, 6.4) * mm, "end": v(0.2, 6.5) * mm});
            skArc(sketch, "E175.0.27", {"start": v(0.2, 6.5) * mm, "mid": v(0, 6.5) * mm, "end": v(-0.2, 6.5) * mm});
            skLineSegment(sketch, "E175.0.28", {"start": v(-0.2, 6.5) * mm, "end": v(-0.3, 6.4) * mm});
            skArc(sketch, "E175.0.29", {"start": v(-0.3, 6.4) * mm, "mid": v(-0.67, 6.36) * mm, "end": v(-1.03, 6.32) * mm});
            skLineSegment(sketch, "E175.0.30", {"start": v(-1.03, 6.32) * mm, "end": v(-1.16, 6.4) * mm});
            skArc(sketch, "E175.0.31", {"start": v(-1.16, 6.4) * mm, "mid": v(-1.35, 6.36) * mm, "end": v(-1.55, 6.31) * mm});
            skLineSegment(sketch, "E175.0.32", {"start": v(-1.55, 6.31) * mm, "end": v(-1.63, 6.19) * mm});
            skArc(sketch, "E175.0.33", {"start": v(-1.63, 6.19) * mm, "mid": v(-1.98, 6.09) * mm, "end": v(-2.32, 5.96) * mm});
            skLineSegment(sketch, "E175.0.34", {"start": v(-2.32, 5.96) * mm, "end": v(-2.46, 6.02) * mm});
            skArc(sketch, "E175.0.35", {"start": v(-2.46, 6.02) * mm, "mid": v(-2.64, 5.94) * mm, "end": v(-2.83, 5.85) * mm});
            skLineSegment(sketch, "E175.0.36", {"start": v(-2.83, 5.85) * mm, "end": v(-2.88, 5.72) * mm});
            skArc(sketch, "E175.0.37", {"start": v(-2.88, 5.72) * mm, "mid": v(-3.2, 5.54) * mm, "end": v(-3.51, 5.35) * mm});
            skLineSegment(sketch, "E175.0.38", {"start": v(-3.51, 5.35) * mm, "end": v(-3.66, 5.37) * mm});
            skArc(sketch, "E175.0.39", {"start": v(-3.66, 5.37) * mm, "mid": v(-3.82, 5.26) * mm, "end": v(-3.98, 5.14) * mm});
            skLineSegment(sketch, "E175.0.40", {"start": v(-3.98, 5.14) * mm, "end": v(-4, 5) * mm});
            skArc(sketch, "E175.0.41", {"start": v(-4, 5) * mm, "mid": v(-4.28, 4.76) * mm, "end": v(-4.55, 4.5) * mm});
            skLineSegment(sketch, "E175.0.42", {"start": v(-4.55, 4.5) * mm, "end": v(-4.7, 4.5) * mm});
            skArc(sketch, "E175.0.43", {"start": v(-4.7, 4.5) * mm, "mid": v(-4.83, 4.35) * mm, "end": v(-4.96, 4.2) * mm});
            skLineSegment(sketch, "E175.0.44", {"start": v(-4.96, 4.2) * mm, "end": v(-4.95, 4.05) * mm});
            skArc(sketch, "E175.0.45", {"start": v(-4.95, 4.05) * mm, "mid": v(-5.18, 3.76) * mm, "end": v(-5.38, 3.46) * mm});
            skLineSegment(sketch, "E175.0.46", {"start": v(-5.38, 3.46) * mm, "end": v(-5.53, 3.42) * mm});
            skArc(sketch, "E175.0.47", {"start": v(-5.53, 3.42) * mm, "mid": v(-5.63, 3.25) * mm, "end": v(-5.73, 3.08) * mm});
            skLineSegment(sketch, "E175.0.48", {"start": v(-5.73, 3.08) * mm, "end": v(-5.69, 2.93) * mm});
            skArc(sketch, "E175.0.49", {"start": v(-5.69, 2.93) * mm, "mid": v(-5.85, 2.6) * mm, "end": v(-5.99, 2.26) * mm});
            skLineSegment(sketch, "E175.0.50", {"start": v(-5.99, 2.26) * mm, "end": v(-6.12, 2.2) * mm});
            skArc(sketch, "E175.0.51", {"start": v(-6.12, 2.2) * mm, "mid": v(-6.18, 2) * mm, "end": v(-6.24, 1.82) * mm});
            skLineSegment(sketch, "E175.0.52", {"start": v(-6.24, 1.82) * mm, "end": v(-6.17, 1.69) * mm});
            skArc(sketch, "E175.0.53", {"start": v(-6.17, 1.69) * mm, "mid": v(-6.26, 1.33) * mm, "end": v(-6.33, 0.97) * mm});
            skLineSegment(sketch, "E175.0.54", {"start": v(-6.33, 0.97) * mm, "end": v(-6.44, 0.88) * mm});
            skArc(sketch, "E175.0.55", {"start": v(-6.44, 0.88) * mm, "mid": v(-6.46, 0.68) * mm, "end": v(-6.48, 0.48) * mm});
            skLineSegment(sketch, "E175.0.56", {"start": v(-6.48, 0.48) * mm, "end": v(-6.39, 0.37) * mm});
            skArc(sketch, "E175.0.57", {"start": v(-6.39, 0.37) * mm, "mid": v(-6.4, 0) * mm, "end": v(-6.39, -0.37) * mm});
            skLineSegment(sketch, "E175.0.58", {"start": v(-6.39, -0.37) * mm, "end": v(-6.48, -0.48) * mm});
            skArc(sketch, "E175.0.59", {"start": v(-6.48, -0.48) * mm, "mid": v(-6.46, -0.68) * mm, "end": v(-6.44, -0.88) * mm});
            skLineSegment(sketch, "E175.0.60", {"start": v(-6.44, -0.88) * mm, "end": v(-6.33, -0.97) * mm});
            skArc(sketch, "E175.0.61", {"start": v(-6.33, -0.97) * mm, "mid": v(-6.26, -1.33) * mm, "end": v(-6.17, -1.69) * mm});
            skLineSegment(sketch, "E175.0.62", {"start": v(-6.17, -1.69) * mm, "end": v(-6.24, -1.82) * mm});
            skArc(sketch, "E175.0.63", {"start": v(-6.24, -1.82) * mm, "mid": v(-6.18, -2) * mm, "end": v(-6.12, -2.2) * mm});
            skLineSegment(sketch, "E175.0.64", {"start": v(-6.12, -2.2) * mm, "end": v(-5.99, -2.26) * mm});
            skArc(sketch, "E175.0.65", {"start": v(-5.99, -2.26) * mm, "mid": v(-5.85, -2.6) * mm, "end": v(-5.69, -2.93) * mm});
            skLineSegment(sketch, "E175.0.66", {"start": v(-5.69, -2.93) * mm, "end": v(-5.73, -3.08) * mm});
            skArc(sketch, "E175.0.67", {"start": v(-5.73, -3.08) * mm, "mid": v(-5.63, -3.25) * mm, "end": v(-5.53, -3.42) * mm});
            skLineSegment(sketch, "E175.0.68", {"start": v(-5.53, -3.42) * mm, "end": v(-5.38, -3.46) * mm});
            skArc(sketch, "E175.0.69", {"start": v(-5.38, -3.46) * mm, "mid": v(-5.18, -3.76) * mm, "end": v(-4.95, -4.05) * mm});
            skLineSegment(sketch, "E175.0.70", {"start": v(-4.95, -4.05) * mm, "end": v(-4.96, -4.2) * mm});
            skArc(sketch, "E175.0.71", {"start": v(-4.96, -4.2) * mm, "mid": v(-4.83, -4.35) * mm, "end": v(-4.7, -4.5) * mm});
            skLineSegment(sketch, "E175.0.72", {"start": v(-4.7, -4.5) * mm, "end": v(-4.55, -4.5) * mm});
            skArc(sketch, "E175.0.73", {"start": v(-4.55, -4.5) * mm, "mid": v(-4.28, -4.76) * mm, "end": v(-4, -5) * mm});
            skLineSegment(sketch, "E175.0.74", {"start": v(-4, -5) * mm, "end": v(-3.98, -5.14) * mm});
            skArc(sketch, "E175.0.75", {"start": v(-3.98, -5.14) * mm, "mid": v(-3.82, -5.26) * mm, "end": v(-3.66, -5.37) * mm});
            skLineSegment(sketch, "E175.0.76", {"start": v(-3.66, -5.37) * mm, "end": v(-3.51, -5.35) * mm});
            skArc(sketch, "E175.0.77", {"start": v(-3.51, -5.35) * mm, "mid": v(-3.2, -5.54) * mm, "end": v(-2.88, -5.72) * mm});
            skLineSegment(sketch, "E175.0.78", {"start": v(-2.88, -5.72) * mm, "end": v(-2.83, -5.85) * mm});
            skArc(sketch, "E175.0.79", {"start": v(-2.83, -5.85) * mm, "mid": v(-2.64, -5.94) * mm, "end": v(-2.46, -6.02) * mm});
            skLineSegment(sketch, "E175.0.80", {"start": v(-2.46, -6.02) * mm, "end": v(-2.32, -5.96) * mm});
            skArc(sketch, "E175.0.81", {"start": v(-2.32, -5.96) * mm, "mid": v(-1.98, -6.09) * mm, "end": v(-1.63, -6.19) * mm});
            skLineSegment(sketch, "E175.0.82", {"start": v(-1.63, -6.19) * mm, "end": v(-1.55, -6.31) * mm});
            skArc(sketch, "E175.0.83", {"start": v(-1.55, -6.31) * mm, "mid": v(-1.35, -6.36) * mm, "end": v(-1.16, -6.4) * mm});
            skLineSegment(sketch, "E175.0.84", {"start": v(-1.16, -6.4) * mm, "end": v(-1.03, -6.32) * mm});
            skArc(sketch, "E175.0.85", {"start": v(-1.03, -6.32) * mm, "mid": v(-0.67, -6.36) * mm, "end": v(-0.3, -6.4) * mm});
            skLineSegment(sketch, "E175.0.86", {"start": v(-0.3, -6.4) * mm, "end": v(-0.2, -6.5) * mm});
            skArc(sketch, "E175.0.87", {"start": v(-0.2, -6.5) * mm, "mid": v(0, -6.5) * mm, "end": v(0.2, -6.5) * mm});
            skLineSegment(sketch, "E175.0.88", {"start": v(0.2, -6.5) * mm, "end": v(0.3, -6.4) * mm});
            skArc(sketch, "E175.0.89", {"start": v(0.3, -6.4) * mm, "mid": v(0.67, -6.36) * mm, "end": v(1.03, -6.32) * mm});
            skLineSegment(sketch, "E175.0.90", {"start": v(1.03, -6.32) * mm, "end": v(1.16, -6.4) * mm});
            skArc(sketch, "E175.0.91", {"start": v(1.16, -6.4) * mm, "mid": v(1.35, -6.36) * mm, "end": v(1.55, -6.31) * mm});
            skLineSegment(sketch, "E175.0.92", {"start": v(1.55, -6.31) * mm, "end": v(1.63, -6.19) * mm});
            skArc(sketch, "E175.0.93", {"start": v(1.63, -6.19) * mm, "mid": v(1.98, -6.09) * mm, "end": v(2.32, -5.96) * mm});
            skLineSegment(sketch, "E175.0.94", {"start": v(2.32, -5.96) * mm, "end": v(2.46, -6.02) * mm});
            skArc(sketch, "E175.0.95", {"start": v(2.46, -6.02) * mm, "mid": v(2.64, -5.94) * mm, "end": v(2.83, -5.85) * mm});
            skLineSegment(sketch, "E175.0.96", {"start": v(2.83, -5.85) * mm, "end": v(2.88, -5.72) * mm});
            skArc(sketch, "E175.0.97", {"start": v(2.88, -5.72) * mm, "mid": v(3.2, -5.54) * mm, "end": v(3.51, -5.35) * mm});
            skLineSegment(sketch, "E175.0.98", {"start": v(3.51, -5.35) * mm, "end": v(3.66, -5.37) * mm});
            skArc(sketch, "E175.0.99", {"start": v(3.66, -5.37) * mm, "mid": v(3.82, -5.26) * mm, "end": v(3.98, -5.14) * mm});
            skLineSegment(sketch, "E175.0.100", {"start": v(3.98, -5.14) * mm, "end": v(4, -5) * mm});
            skArc(sketch, "E175.0.101", {"start": v(4, -5) * mm, "mid": v(4.28, -4.76) * mm, "end": v(4.55, -4.5) * mm});
            skLineSegment(sketch, "E175.0.102", {"start": v(4.55, -4.5) * mm, "end": v(4.7, -4.5) * mm});
            skArc(sketch, "E175.0.103", {"start": v(4.7, -4.5) * mm, "mid": v(4.83, -4.35) * mm, "end": v(4.96, -4.2) * mm});
            skLineSegment(sketch, "E175.0.104", {"start": v(4.96, -4.2) * mm, "end": v(4.95, -4.05) * mm});
            skArc(sketch, "E175.0.105", {"start": v(4.95, -4.05) * mm, "mid": v(5.18, -3.76) * mm, "end": v(5.38, -3.46) * mm});
            skLineSegment(sketch, "E175.0.106", {"start": v(5.38, -3.46) * mm, "end": v(5.53, -3.42) * mm});
            skArc(sketch, "E175.0.107", {"start": v(5.53, -3.42) * mm, "mid": v(5.63, -3.25) * mm, "end": v(5.73, -3.08) * mm});
            skLineSegment(sketch, "E175.0.108", {"start": v(5.73, -3.08) * mm, "end": v(5.69, -2.93) * mm});
            skArc(sketch, "E175.0.109", {"start": v(5.69, -2.93) * mm, "mid": v(5.85, -2.6) * mm, "end": v(5.99, -2.26) * mm});
            skLineSegment(sketch, "E175.0.110", {"start": v(5.99, -2.26) * mm, "end": v(6.12, -2.2) * mm});
            skArc(sketch, "E175.0.111", {"start": v(6.12, -2.2) * mm, "mid": v(6.18, -2) * mm, "end": v(6.24, -1.82) * mm});
            skLineSegment(sketch, "E175.0.112", {"start": v(6.24, -1.82) * mm, "end": v(6.17, -1.69) * mm});
            skArc(sketch, "E175.0.113", {"start": v(6.17, -1.69) * mm, "mid": v(6.26, -1.33) * mm, "end": v(6.33, -0.97) * mm});
            skLineSegment(sketch, "E175.0.114", {"start": v(6.33, -0.97) * mm, "end": v(6.44, -0.88) * mm});
            skArc(sketch, "E175.0.115", {"start": v(6.44, -0.88) * mm, "mid": v(6.46, -0.68) * mm, "end": v(6.48, -0.48) * mm});
            skLineSegment(sketch, "E175.0.116", {"start": v(6.48, -0.48) * mm, "end": v(6.39, -0.37) * mm});
            skArc(sketch, "E175.0.117", {"start": v(6.39, -0.37) * mm, "mid": v(6.4, 0) * mm, "end": v(6.39, 0.37) * mm});
            skLineSegment(sketch, "E175.0.118", {"start": v(6.39, 0.37) * mm, "end": v(6.48, 0.48) * mm});
            skArc(sketch, "E175.0.119", {"start": v(6.48, 0.48) * mm, "mid": v(6.46, 0.68) * mm, "end": v(6.44, 0.88) * mm});
            skSolve(sketch);
        }
        {
            var Q0;
            Q0=makeQuery(id+"F5.imprint","IMPRINT",FACE,{"disambiguationData":[TD([[makeQuery(id+"F5.imprint","IMPRINT",EDGE,{"derivedFrom":sQuery(id+"F5.wireOp",EDGE,"E174")}),-1.0]])]});
            extrude(context, id + "F6", {"entities" : qUnion([Q0]), "operationType" : NewBodyOperationType.ADD, "depth" : (getVariable(context, 'Bore_Depth_F')) * mm});
        }
        {
            var Q0;
            Q0=makeQuery(id+"F4.opExtrude","CAP_FACE",FACE,{"disambiguationData":[OSD([sQuery(id+"F3.wireOp",EDGE,"E0"),sQuery(id+"F3.wireOp",EDGE,"E1"),sQuery(id+"F3.wireOp",EDGE,"E2"),sQuery(id+"F3.wireOp",EDGE,"E3"),sQuery(id+"F3.wireOp",EDGE,"E4"),sQuery(id+"F3.wireOp",EDGE,"E5"),sQuery(id+"F3.wireOp",EDGE,"E6"),sQuery(id+"F3.wireOp",EDGE,"E7"),sQuery(id+"F3.wireOp",EDGE,"E8"),sQuery(id+"F3.wireOp",EDGE,"E9"),sQuery(id+"F3.wireOp",EDGE,"E10"),sQuery(id+"F3.wireOp",EDGE,"E11"),sQuery(id+"F3.wireOp",EDGE,"E12"),sQuery(id+"F3.wireOp",EDGE,"E13"),sQuery(id+"F3.wireOp",EDGE,"E14"),sQuery(id+"F3.wireOp",EDGE,"E15"),sQuery(id+"F3.wireOp",EDGE,"E16"),sQuery(id+"F3.wireOp",EDGE,"E17"),sQuery(id+"F3.wireOp",EDGE,"E18"),sQuery(id+"F3.wireOp",EDGE,"E19"),sQuery(id+"F3.wireOp",EDGE,"E20"),sQuery(id+"F3.wireOp",EDGE,"E21"),sQuery(id+"F3.wireOp",EDGE,"E22"),sQuery(id+"F3.wireOp",EDGE,"E23"),sQuery(id+"F3.wireOp",EDGE,"E24"),sQuery(id+"F3.wireOp",EDGE,"E25"),sQuery(id+"F3.wireOp",EDGE,"E26"),sQuery(id+"F3.wireOp",EDGE,"E27"),sQuery(id+"F3.wireOp",EDGE,"E28"),sQuery(id+"F3.wireOp",EDGE,"E29"),sQuery(id+"F3.wireOp",EDGE,"E30"),sQuery(id+"F3.wireOp",EDGE,"E31"),sQuery(id+"F3.wireOp",EDGE,"E32"),sQuery(id+"F3.wireOp",EDGE,"E33"),sQuery(id+"F3.wireOp",EDGE,"E34"),sQuery(id+"F3.wireOp",EDGE,"E35"),sQuery(id+"F3.wireOp",EDGE,"E36"),sQuery(id+"F3.wireOp",EDGE,"E37"),sQuery(id+"F3.wireOp",EDGE,"E38"),sQuery(id+"F3.wireOp",EDGE,"E39"),sQuery(id+"F3.wireOp",EDGE,"E40"),sQuery(id+"F3.wireOp",EDGE,"E41"),sQuery(id+"F3.wireOp",EDGE,"E42"),sQuery(id+"F3.wireOp",EDGE,"E43"),sQuery(id+"F3.wireOp",EDGE,"E44"),sQuery(id+"F3.wireOp",EDGE,"E45"),sQuery(id+"F3.wireOp",EDGE,"E46"),sQuery(id+"F3.wireOp",EDGE,"E47"),sQuery(id+"F3.wireOp",EDGE,"E48"),sQuery(id+"F3.wireOp",EDGE,"E49"),sQuery(id+"F3.wireOp",EDGE,"E50"),sQuery(id+"F3.wireOp",EDGE,"E51"),sQuery(id+"F3.wireOp",EDGE,"E52"),sQuery(id+"F3.wireOp",EDGE,"E53"),sQuery(id+"F3.wireOp",EDGE,"E54"),sQuery(id+"F3.wireOp",EDGE,"E55"),sQuery(id+"F3.wireOp",EDGE,"E56"),sQuery(id+"F3.wireOp",EDGE,"E57"),sQuery(id+"F3.wireOp",EDGE,"E58"),sQuery(id+"F3.wireOp",EDGE,"E59"),sQuery(id+"F3.wireOp",EDGE,"E60"),sQuery(id+"F3.wireOp",EDGE,"E61"),sQuery(id+"F3.wireOp",EDGE,"E62"),sQuery(id+"F3.wireOp",EDGE,"E63"),sQuery(id+"F3.wireOp",EDGE,"E64"),sQuery(id+"F3.wireOp",EDGE,"E65"),sQuery(id+"F3.wireOp",EDGE,"E66"),sQuery(id+"F3.wireOp",EDGE,"E67"),sQuery(id+"F3.wireOp",EDGE,"E68"),sQuery(id+"F3.wireOp",EDGE,"E69"),sQuery(id+"F3.wireOp",EDGE,"E70"),sQuery(id+"F3.wireOp",EDGE,"E71"),sQuery(id+"F3.wireOp",EDGE,"E72"),sQuery(id+"F3.wireOp",EDGE,"E73"),sQuery(id+"F3.wireOp",EDGE,"E74"),sQuery(id+"F3.wireOp",EDGE,"E75"),sQuery(id+"F3.wireOp",EDGE,"E76"),sQuery(id+"F3.wireOp",EDGE,"E77"),sQuery(id+"F3.wireOp",EDGE,"E78"),sQuery(id+"F3.wireOp",EDGE,"E79"),sQuery(id+"F3.wireOp",EDGE,"E80"),sQuery(id+"F3.wireOp",EDGE,"E81"),sQuery(id+"F3.wireOp",EDGE,"E82"),sQuery(id+"F3.wireOp",EDGE,"E83"),sQuery(id+"F3.wireOp",EDGE,"E84"),sQuery(id+"F3.wireOp",EDGE,"E85"),sQuery(id+"F3.wireOp",EDGE,"E86"),sQuery(id+"F3.wireOp",EDGE,"E87"),sQuery(id+"F3.wireOp",EDGE,"E88"),sQuery(id+"F3.wireOp",EDGE,"E89"),sQuery(id+"F3.wireOp",EDGE,"E90"),sQuery(id+"F3.wireOp",EDGE,"E91"),sQuery(id+"F3.wireOp",EDGE,"E92"),sQuery(id+"F3.wireOp",EDGE,"E93"),sQuery(id+"F3.wireOp",EDGE,"E94"),sQuery(id+"F3.wireOp",EDGE,"E95"),sQuery(id+"F3.wireOp",EDGE,"E96"),sQuery(id+"F3.wireOp",EDGE,"E97"),sQuery(id+"F3.wireOp",EDGE,"E98"),sQuery(id+"F3.wireOp",EDGE,"E99"),sQuery(id+"F3.wireOp",EDGE,"E100"),sQuery(id+"F3.wireOp",EDGE,"E101"),sQuery(id+"F3.wireOp",EDGE,"E102"),sQuery(id+"F3.wireOp",EDGE,"E103"),sQuery(id+"F3.wireOp",EDGE,"E104"),sQuery(id+"F3.wireOp",EDGE,"E105"),sQuery(id+"F3.wireOp",EDGE,"E106"),sQuery(id+"F3.wireOp",EDGE,"E107"),sQuery(id+"F3.wireOp",EDGE,"E108"),sQuery(id+"F3.wireOp",EDGE,"E109"),sQuery(id+"F3.wireOp",EDGE,"E110"),sQuery(id+"F3.wireOp",EDGE,"E111"),sQuery(id+"F3.wireOp",EDGE,"E112"),sQuery(id+"F3.wireOp",EDGE,"E113"),sQuery(id+"F3.wireOp",EDGE,"E114"),sQuery(id+"F3.wireOp",EDGE,"E115"),sQuery(id+"F3.wireOp",EDGE,"E116"),sQuery(id+"F3.wireOp",EDGE,"E117"),sQuery(id+"F3.wireOp",EDGE,"E118"),sQuery(id+"F3.wireOp",EDGE,"E119"),sQuery(id+"F3.wireOp",EDGE,"E120"),sQuery(id+"F3.wireOp",EDGE,"E121"),sQuery(id+"F3.wireOp",EDGE,"E122"),sQuery(id+"F3.wireOp",EDGE,"E123"),sQuery(id+"F3.wireOp",EDGE,"E124"),sQuery(id+"F3.wireOp",EDGE,"E125"),sQuery(id+"F3.wireOp",EDGE,"E126"),sQuery(id+"F3.wireOp",EDGE,"E127"),sQuery(id+"F3.wireOp",EDGE,"E128"),sQuery(id+"F3.wireOp",EDGE,"E129"),sQuery(id+"F3.wireOp",EDGE,"E130"),sQuery(id+"F3.wireOp",EDGE,"E131"),sQuery(id+"F3.wireOp",EDGE,"E132"),sQuery(id+"F3.wireOp",EDGE,"E133"),sQuery(id+"F3.wireOp",EDGE,"E134"),sQuery(id+"F3.wireOp",EDGE,"E135"),sQuery(id+"F3.wireOp",EDGE,"E136"),sQuery(id+"F3.wireOp",EDGE,"E137"),sQuery(id+"F3.wireOp",EDGE,"E138"),sQuery(id+"F3.wireOp",EDGE,"E139"),sQuery(id+"F3.wireOp",EDGE,"E140"),sQuery(id+"F3.wireOp",EDGE,"E141"),sQuery(id+"F3.wireOp",EDGE,"E142"),sQuery(id+"F3.wireOp",EDGE,"E143"),sQuery(id+"F3.wireOp",EDGE,"E144"),sQuery(id+"F3.wireOp",EDGE,"E145"),sQuery(id+"F3.wireOp",EDGE,"E146"),sQuery(id+"F3.wireOp",EDGE,"E147"),sQuery(id+"F3.wireOp",EDGE,"E148"),sQuery(id+"F3.wireOp",EDGE,"E149"),sQuery(id+"F3.wireOp",EDGE,"E150"),sQuery(id+"F3.wireOp",EDGE,"E151"),sQuery(id+"F3.wireOp",EDGE,"E152"),sQuery(id+"F3.wireOp",EDGE,"E153"),sQuery(id+"F3.wireOp",EDGE,"E154"),sQuery(id+"F3.wireOp",EDGE,"E155"),sQuery(id+"F3.wireOp",EDGE,"E156"),sQuery(id+"F3.wireOp",EDGE,"E157"),sQuery(id+"F3.wireOp",EDGE,"E158"),sQuery(id+"F3.wireOp",EDGE,"E159"),sQuery(id+"F3.wireOp",EDGE,"E160"),sQuery(id+"F3.wireOp",EDGE,"E161"),sQuery(id+"F3.wireOp",EDGE,"E162"),sQuery(id+"F3.wireOp",EDGE,"E163"),sQuery(id+"F3.wireOp",EDGE,"E164"),sQuery(id+"F3.wireOp",EDGE,"E165"),sQuery(id+"F3.wireOp",EDGE,"E166"),sQuery(id+"F3.wireOp",EDGE,"E167"),sQuery(id+"F3.wireOp",EDGE,"E168"),sQuery(id+"F3.wireOp",EDGE,"E169"),sQuery(id+"F3.wireOp",EDGE,"E170"),sQuery(id+"F3.wireOp",EDGE,"E171"),sQuery(id+"F3.wireOp",EDGE,"E172"),sQuery(id+"F3.wireOp",EDGE,"E173")])],"isStart":true});
            var sketch = newSketch(context, id + "F7", { "sketchPlane" : qUnion([Q0])});
            skCircle(sketch, "E176", {"center": v(0, 0) * mm, "radius": 5.75 * mm});
            skLineSegment(sketch, "E177.0.0", {"start": v(-6.33, 0.97) * mm, "end": v(-6.44, 0.88) * mm});
            skArc(sketch, "E177.0.1", {"start": v(-6.44, 0.88) * mm, "mid": v(-6.46, 0.68) * mm, "end": v(-6.48, 0.48) * mm});
            skLineSegment(sketch, "E177.0.2", {"start": v(-6.48, 0.48) * mm, "end": v(-6.39, 0.37) * mm});
            skArc(sketch, "E177.0.3", {"start": v(-6.39, 0.37) * mm, "mid": v(-6.4, 0) * mm, "end": v(-6.39, -0.37) * mm});
            skLineSegment(sketch, "E177.0.4", {"start": v(-6.39, -0.37) * mm, "end": v(-6.48, -0.48) * mm});
            skArc(sketch, "E177.0.5", {"start": v(-6.48, -0.48) * mm, "mid": v(-6.46, -0.68) * mm, "end": v(-6.44, -0.88) * mm});
            skLineSegment(sketch, "E177.0.6", {"start": v(-6.44, -0.88) * mm, "end": v(-6.33, -0.97) * mm});
            skArc(sketch, "E177.0.7", {"start": v(-6.33, -0.97) * mm, "mid": v(-6.26, -1.33) * mm, "end": v(-6.17, -1.69) * mm});
            skLineSegment(sketch, "E177.0.8", {"start": v(-6.17, -1.69) * mm, "end": v(-6.24, -1.82) * mm});
            skArc(sketch, "E177.0.9", {"start": v(-6.24, -1.82) * mm, "mid": v(-6.18, -2) * mm, "end": v(-6.12, -2.2) * mm});
            skLineSegment(sketch, "E177.0.10", {"start": v(-6.12, -2.2) * mm, "end": v(-5.99, -2.26) * mm});
            skArc(sketch, "E177.0.11", {"start": v(-5.99, -2.26) * mm, "mid": v(-5.85, -2.6) * mm, "end": v(-5.69, -2.93) * mm});
            skLineSegment(sketch, "E177.0.12", {"start": v(-5.69, -2.93) * mm, "end": v(-5.73, -3.08) * mm});
            skArc(sketch, "E177.0.13", {"start": v(-5.73, -3.08) * mm, "mid": v(-5.63, -3.25) * mm, "end": v(-5.53, -3.42) * mm});
            skLineSegment(sketch, "E177.0.14", {"start": v(-5.53, -3.42) * mm, "end": v(-5.38, -3.46) * mm});
            skArc(sketch, "E177.0.15", {"start": v(-5.38, -3.46) * mm, "mid": v(-5.18, -3.76) * mm, "end": v(-4.95, -4.05) * mm});
            skLineSegment(sketch, "E177.0.16", {"start": v(-4.95, -4.05) * mm, "end": v(-4.96, -4.2) * mm});
            skArc(sketch, "E177.0.17", {"start": v(-4.96, -4.2) * mm, "mid": v(-4.83, -4.35) * mm, "end": v(-4.7, -4.5) * mm});
            skLineSegment(sketch, "E177.0.18", {"start": v(-4.7, -4.5) * mm, "end": v(-4.55, -4.5) * mm});
            skArc(sketch, "E177.0.19", {"start": v(-4.55, -4.5) * mm, "mid": v(-4.28, -4.76) * mm, "end": v(-4, -5) * mm});
            skLineSegment(sketch, "E177.0.20", {"start": v(-4, -5) * mm, "end": v(-3.98, -5.14) * mm});
            skArc(sketch, "E177.0.21", {"start": v(-3.98, -5.14) * mm, "mid": v(-3.82, -5.26) * mm, "end": v(-3.66, -5.37) * mm});
            skLineSegment(sketch, "E177.0.22", {"start": v(-3.66, -5.37) * mm, "end": v(-3.51, -5.35) * mm});
            skArc(sketch, "E177.0.23", {"start": v(-3.51, -5.35) * mm, "mid": v(-3.2, -5.54) * mm, "end": v(-2.88, -5.72) * mm});
            skLineSegment(sketch, "E177.0.24", {"start": v(-2.88, -5.72) * mm, "end": v(-2.83, -5.85) * mm});
            skArc(sketch, "E177.0.25", {"start": v(-2.83, -5.85) * mm, "mid": v(-2.64, -5.94) * mm, "end": v(-2.46, -6.02) * mm});
            skLineSegment(sketch, "E177.0.26", {"start": v(-2.46, -6.02) * mm, "end": v(-2.32, -5.96) * mm});
            skArc(sketch, "E177.0.27", {"start": v(-2.32, -5.96) * mm, "mid": v(-1.98, -6.09) * mm, "end": v(-1.63, -6.19) * mm});
            skLineSegment(sketch, "E177.0.28", {"start": v(-1.63, -6.19) * mm, "end": v(-1.55, -6.31) * mm});
            skArc(sketch, "E177.0.29", {"start": v(-1.55, -6.31) * mm, "mid": v(-1.35, -6.36) * mm, "end": v(-1.16, -6.4) * mm});
            skLineSegment(sketch, "E177.0.30", {"start": v(-1.16, -6.4) * mm, "end": v(-1.03, -6.32) * mm});
            skArc(sketch, "E177.0.31", {"start": v(-1.03, -6.32) * mm, "mid": v(-0.67, -6.36) * mm, "end": v(-0.3, -6.4) * mm});
            skLineSegment(sketch, "E177.0.32", {"start": v(-0.3, -6.4) * mm, "end": v(-0.2, -6.5) * mm});
            skArc(sketch, "E177.0.33", {"start": v(-0.2, -6.5) * mm, "mid": v(0, -6.5) * mm, "end": v(0.2, -6.5) * mm});
            skLineSegment(sketch, "E177.0.34", {"start": v(0.2, -6.5) * mm, "end": v(0.3, -6.4) * mm});
            skArc(sketch, "E177.0.35", {"start": v(0.3, -6.4) * mm, "mid": v(0.67, -6.36) * mm, "end": v(1.03, -6.32) * mm});
            skLineSegment(sketch, "E177.0.36", {"start": v(1.03, -6.32) * mm, "end": v(1.16, -6.4) * mm});
            skArc(sketch, "E177.0.37", {"start": v(1.16, -6.4) * mm, "mid": v(1.35, -6.36) * mm, "end": v(1.55, -6.31) * mm});
            skLineSegment(sketch, "E177.0.38", {"start": v(1.55, -6.31) * mm, "end": v(1.63, -6.19) * mm});
            skArc(sketch, "E177.0.39", {"start": v(1.63, -6.19) * mm, "mid": v(1.98, -6.09) * mm, "end": v(2.32, -5.96) * mm});
            skLineSegment(sketch, "E177.0.40", {"start": v(2.32, -5.96) * mm, "end": v(2.46, -6.02) * mm});
            skArc(sketch, "E177.0.41", {"start": v(2.46, -6.02) * mm, "mid": v(2.64, -5.94) * mm, "end": v(2.83, -5.85) * mm});
            skLineSegment(sketch, "E177.0.42", {"start": v(2.83, -5.85) * mm, "end": v(2.88, -5.72) * mm});
            skArc(sketch, "E177.0.43", {"start": v(2.88, -5.72) * mm, "mid": v(3.2, -5.54) * mm, "end": v(3.51, -5.35) * mm});
            skLineSegment(sketch, "E177.0.44", {"start": v(3.51, -5.35) * mm, "end": v(3.66, -5.37) * mm});
            skArc(sketch, "E177.0.45", {"start": v(3.66, -5.37) * mm, "mid": v(3.82, -5.26) * mm, "end": v(3.98, -5.14) * mm});
            skLineSegment(sketch, "E177.0.46", {"start": v(3.98, -5.14) * mm, "end": v(4, -5) * mm});
            skArc(sketch, "E177.0.47", {"start": v(4, -5) * mm, "mid": v(4.28, -4.76) * mm, "end": v(4.55, -4.5) * mm});
            skLineSegment(sketch, "E177.0.48", {"start": v(4.55, -4.5) * mm, "end": v(4.7, -4.5) * mm});
            skArc(sketch, "E177.0.49", {"start": v(4.7, -4.5) * mm, "mid": v(4.83, -4.35) * mm, "end": v(4.96, -4.2) * mm});
            skLineSegment(sketch, "E177.0.50", {"start": v(4.96, -4.2) * mm, "end": v(4.95, -4.05) * mm});
            skArc(sketch, "E177.0.51", {"start": v(4.95, -4.05) * mm, "mid": v(5.18, -3.76) * mm, "end": v(5.38, -3.46) * mm});
            skLineSegment(sketch, "E177.0.52", {"start": v(5.38, -3.46) * mm, "end": v(5.53, -3.42) * mm});
            skArc(sketch, "E177.0.53", {"start": v(5.53, -3.42) * mm, "mid": v(5.63, -3.25) * mm, "end": v(5.73, -3.08) * mm});
            skLineSegment(sketch, "E177.0.54", {"start": v(5.73, -3.08) * mm, "end": v(5.69, -2.93) * mm});
            skArc(sketch, "E177.0.55", {"start": v(5.69, -2.93) * mm, "mid": v(5.85, -2.6) * mm, "end": v(5.99, -2.26) * mm});
            skLineSegment(sketch, "E177.0.56", {"start": v(5.99, -2.26) * mm, "end": v(6.12, -2.2) * mm});
            skArc(sketch, "E177.0.57", {"start": v(6.12, -2.2) * mm, "mid": v(6.18, -2) * mm, "end": v(6.24, -1.82) * mm});
            skLineSegment(sketch, "E177.0.58", {"start": v(6.24, -1.82) * mm, "end": v(6.17, -1.69) * mm});
            skArc(sketch, "E177.0.59", {"start": v(6.17, -1.69) * mm, "mid": v(6.26, -1.33) * mm, "end": v(6.33, -0.97) * mm});
            skLineSegment(sketch, "E177.0.60", {"start": v(6.33, -0.97) * mm, "end": v(6.44, -0.88) * mm});
            skArc(sketch, "E177.0.61", {"start": v(6.44, -0.88) * mm, "mid": v(6.46, -0.68) * mm, "end": v(6.48, -0.48) * mm});
            skLineSegment(sketch, "E177.0.62", {"start": v(6.48, -0.48) * mm, "end": v(6.39, -0.37) * mm});
            skArc(sketch, "E177.0.63", {"start": v(6.39, -0.37) * mm, "mid": v(6.4, 0) * mm, "end": v(6.39, 0.37) * mm});
            skLineSegment(sketch, "E177.0.64", {"start": v(6.39, 0.37) * mm, "end": v(6.48, 0.48) * mm});
            skArc(sketch, "E177.0.65", {"start": v(6.48, 0.48) * mm, "mid": v(6.46, 0.68) * mm, "end": v(6.44, 0.88) * mm});
            skLineSegment(sketch, "E177.0.66", {"start": v(6.44, 0.88) * mm, "end": v(6.33, 0.97) * mm});
            skArc(sketch, "E177.0.67", {"start": v(6.33, 0.97) * mm, "mid": v(6.26, 1.33) * mm, "end": v(6.17, 1.69) * mm});
            skLineSegment(sketch, "E177.0.68", {"start": v(6.17, 1.69) * mm, "end": v(6.24, 1.82) * mm});
            skArc(sketch, "E177.0.69", {"start": v(6.24, 1.82) * mm, "mid": v(6.18, 2) * mm, "end": v(6.12, 2.2) * mm});
            skLineSegment(sketch, "E177.0.70", {"start": v(6.12, 2.2) * mm, "end": v(5.99, 2.26) * mm});
            skArc(sketch, "E177.0.71", {"start": v(5.99, 2.26) * mm, "mid": v(5.85, 2.6) * mm, "end": v(5.69, 2.93) * mm});
            skLineSegment(sketch, "E177.0.72", {"start": v(5.69, 2.93) * mm, "end": v(5.73, 3.08) * mm});
            skArc(sketch, "E177.0.73", {"start": v(5.73, 3.08) * mm, "mid": v(5.63, 3.25) * mm, "end": v(5.53, 3.42) * mm});
            skLineSegment(sketch, "E177.0.74", {"start": v(5.53, 3.42) * mm, "end": v(5.38, 3.46) * mm});
            skArc(sketch, "E177.0.75", {"start": v(5.38, 3.46) * mm, "mid": v(5.18, 3.76) * mm, "end": v(4.95, 4.05) * mm});
            skLineSegment(sketch, "E177.0.76", {"start": v(4.95, 4.05) * mm, "end": v(4.96, 4.2) * mm});
            skArc(sketch, "E177.0.77", {"start": v(4.96, 4.2) * mm, "mid": v(4.83, 4.35) * mm, "end": v(4.7, 4.5) * mm});
            skLineSegment(sketch, "E177.0.78", {"start": v(4.7, 4.5) * mm, "end": v(4.55, 4.5) * mm});
            skArc(sketch, "E177.0.79", {"start": v(4.55, 4.5) * mm, "mid": v(4.28, 4.76) * mm, "end": v(4, 5) * mm});
            skLineSegment(sketch, "E177.0.80", {"start": v(4, 5) * mm, "end": v(3.98, 5.14) * mm});
            skArc(sketch, "E177.0.81", {"start": v(3.98, 5.14) * mm, "mid": v(3.82, 5.26) * mm, "end": v(3.66, 5.37) * mm});
            skLineSegment(sketch, "E177.0.82", {"start": v(3.66, 5.37) * mm, "end": v(3.51, 5.35) * mm});
            skArc(sketch, "E177.0.83", {"start": v(3.51, 5.35) * mm, "mid": v(3.2, 5.54) * mm, "end": v(2.88, 5.72) * mm});
            skLineSegment(sketch, "E177.0.84", {"start": v(2.88, 5.72) * mm, "end": v(2.83, 5.85) * mm});
            skArc(sketch, "E177.0.85", {"start": v(2.83, 5.85) * mm, "mid": v(2.64, 5.94) * mm, "end": v(2.46, 6.02) * mm});
            skLineSegment(sketch, "E177.0.86", {"start": v(2.46, 6.02) * mm, "end": v(2.32, 5.96) * mm});
            skArc(sketch, "E177.0.87", {"start": v(2.32, 5.96) * mm, "mid": v(1.98, 6.09) * mm, "end": v(1.63, 6.19) * mm});
            skLineSegment(sketch, "E177.0.88", {"start": v(1.63, 6.19) * mm, "end": v(1.55, 6.31) * mm});
            skArc(sketch, "E177.0.89", {"start": v(1.55, 6.31) * mm, "mid": v(1.35, 6.36) * mm, "end": v(1.16, 6.4) * mm});
            skLineSegment(sketch, "E177.0.90", {"start": v(1.16, 6.4) * mm, "end": v(1.03, 6.32) * mm});
            skArc(sketch, "E177.0.91", {"start": v(1.03, 6.32) * mm, "mid": v(0.67, 6.36) * mm, "end": v(0.3, 6.4) * mm});
            skLineSegment(sketch, "E177.0.92", {"start": v(0.3, 6.4) * mm, "end": v(0.2, 6.5) * mm});
            skArc(sketch, "E177.0.93", {"start": v(0.2, 6.5) * mm, "mid": v(0, 6.5) * mm, "end": v(-0.2, 6.5) * mm});
            skLineSegment(sketch, "E177.0.94", {"start": v(-0.2, 6.5) * mm, "end": v(-0.3, 6.4) * mm});
            skArc(sketch, "E177.0.95", {"start": v(-0.3, 6.4) * mm, "mid": v(-0.67, 6.36) * mm, "end": v(-1.03, 6.32) * mm});
            skLineSegment(sketch, "E177.0.96", {"start": v(-1.03, 6.32) * mm, "end": v(-1.16, 6.4) * mm});
            skArc(sketch, "E177.0.97", {"start": v(-1.16, 6.4) * mm, "mid": v(-1.35, 6.36) * mm, "end": v(-1.55, 6.31) * mm});
            skLineSegment(sketch, "E177.0.98", {"start": v(-1.55, 6.31) * mm, "end": v(-1.63, 6.19) * mm});
            skArc(sketch, "E177.0.99", {"start": v(-1.63, 6.19) * mm, "mid": v(-1.98, 6.09) * mm, "end": v(-2.32, 5.96) * mm});
            skLineSegment(sketch, "E177.0.100", {"start": v(-2.32, 5.96) * mm, "end": v(-2.46, 6.02) * mm});
            skArc(sketch, "E177.0.101", {"start": v(-2.46, 6.02) * mm, "mid": v(-2.64, 5.94) * mm, "end": v(-2.83, 5.85) * mm});
            skLineSegment(sketch, "E177.0.102", {"start": v(-2.83, 5.85) * mm, "end": v(-2.88, 5.72) * mm});
            skArc(sketch, "E177.0.103", {"start": v(-2.88, 5.72) * mm, "mid": v(-3.2, 5.54) * mm, "end": v(-3.51, 5.35) * mm});
            skLineSegment(sketch, "E177.0.104", {"start": v(-3.51, 5.35) * mm, "end": v(-3.66, 5.37) * mm});
            skArc(sketch, "E177.0.105", {"start": v(-3.66, 5.37) * mm, "mid": v(-3.82, 5.26) * mm, "end": v(-3.98, 5.14) * mm});
            skLineSegment(sketch, "E177.0.106", {"start": v(-3.98, 5.14) * mm, "end": v(-4, 5) * mm});
            skArc(sketch, "E177.0.107", {"start": v(-4, 5) * mm, "mid": v(-4.28, 4.76) * mm, "end": v(-4.55, 4.5) * mm});
            skLineSegment(sketch, "E177.0.108", {"start": v(-4.55, 4.5) * mm, "end": v(-4.7, 4.5) * mm});
            skArc(sketch, "E177.0.109", {"start": v(-4.7, 4.5) * mm, "mid": v(-4.83, 4.35) * mm, "end": v(-4.96, 4.2) * mm});
            skLineSegment(sketch, "E177.0.110", {"start": v(-4.96, 4.2) * mm, "end": v(-4.95, 4.05) * mm});
            skArc(sketch, "E177.0.111", {"start": v(-4.95, 4.05) * mm, "mid": v(-5.18, 3.76) * mm, "end": v(-5.38, 3.46) * mm});
            skLineSegment(sketch, "E177.0.112", {"start": v(-5.38, 3.46) * mm, "end": v(-5.53, 3.42) * mm});
            skArc(sketch, "E177.0.113", {"start": v(-5.53, 3.42) * mm, "mid": v(-5.63, 3.25) * mm, "end": v(-5.73, 3.08) * mm});
            skLineSegment(sketch, "E177.0.114", {"start": v(-5.73, 3.08) * mm, "end": v(-5.69, 2.93) * mm});
            skArc(sketch, "E177.0.115", {"start": v(-5.69, 2.93) * mm, "mid": v(-5.85, 2.6) * mm, "end": v(-5.99, 2.26) * mm});
            skLineSegment(sketch, "E177.0.116", {"start": v(-5.99, 2.26) * mm, "end": v(-6.12, 2.2) * mm});
            skArc(sketch, "E177.0.117", {"start": v(-6.12, 2.2) * mm, "mid": v(-6.18, 2) * mm, "end": v(-6.24, 1.82) * mm});
            skLineSegment(sketch, "E177.0.118", {"start": v(-6.24, 1.82) * mm, "end": v(-6.17, 1.69) * mm});
            skArc(sketch, "E177.0.119", {"start": v(-6.17, 1.69) * mm, "mid": v(-6.26, 1.33) * mm, "end": v(-6.33, 0.97) * mm});
            skSolve(sketch);
        }
        {
            var Q0;
            Q0=makeQuery(id+"F7.imprint","IMPRINT",FACE,{"disambiguationData":[TD([[makeQuery(id+"F7.imprint","IMPRINT",EDGE,{"derivedFrom":sQuery(id+"F7.wireOp",EDGE,"E176")}),-1.0]])]});
            extrude(context, id + "F8", {"entities" : qUnion([Q0]), "operationType" : NewBodyOperationType.ADD, "depth" : (getVariable(context, 'Bore_Depth_R')) * mm});
        }
        {
            var Q0;
            Q0=qCreatedBy(makeId("Right.planeOp"),FACE);
            var sketch = newSketch(context, id + "F9", { "sketchPlane" : qUnion([Q0])});
            skCircle(sketch, "E178", {"center": v(-83, 0) * mm, "radius": 3.25 * mm});
            skPoint(sketch, "E179", {"position": v(-56.13, 0) * mm});
            skCircle(sketch, "E180", {"center": v(26, 0) * mm, "radius": 1.25 * mm});
            skCircle(sketch, "E181", {"center": v(-92, 0) * mm, "radius": 1.25 * mm});
            skSolve(sketch);
        }
        {
            var Q0;
            Q0=makeQuery(id+"F9.imprint","IMPRINT",FACE,{"disambiguationData":[TD([[makeQuery(id+"F9.imprint","IMPRINT",EDGE,{"derivedFrom":sQuery(id+"F9.wireOp",EDGE,"E178")}),1.0]])]});
            var Q1;
            Q1=makeQuery(id+"F9.imprint","IMPRINT",FACE,{"disambiguationData":[TD([[makeQuery(id+"F9.imprint","IMPRINT",EDGE,{"derivedFrom":sQuery(id+"F9.wireOp",EDGE,"E181")}),1.0]])]});
            extrude(context, id + "F10", {"entities" : qUnion([Q0, Q1]), "operationType" : NewBodyOperationType.REMOVE, "endBound" : BoundingType.THROUGH_ALL, "oppositeDirection" : true, "depth" : 5 * mm});
        }
        {
            var Q0;
            Q0=makeQuery(id+"F4.opExtrude","SWEPT_BODY",BODY,{"disambiguationData":[OSD([sQuery(id+"F3.wireOp",EDGE,"E0"),sQuery(id+"F3.wireOp",EDGE,"E1"),sQuery(id+"F3.wireOp",EDGE,"E2"),sQuery(id+"F3.wireOp",EDGE,"E3"),sQuery(id+"F3.wireOp",EDGE,"E4"),sQuery(id+"F3.wireOp",EDGE,"E5"),sQuery(id+"F3.wireOp",EDGE,"E6"),sQuery(id+"F3.wireOp",EDGE,"E7"),sQuery(id+"F3.wireOp",EDGE,"E8"),sQuery(id+"F3.wireOp",EDGE,"E9"),sQuery(id+"F3.wireOp",EDGE,"E10"),sQuery(id+"F3.wireOp",EDGE,"E11"),sQuery(id+"F3.wireOp",EDGE,"E12"),sQuery(id+"F3.wireOp",EDGE,"E13"),sQuery(id+"F3.wireOp",EDGE,"E14"),sQuery(id+"F3.wireOp",EDGE,"E15"),sQuery(id+"F3.wireOp",EDGE,"E16"),sQuery(id+"F3.wireOp",EDGE,"E17"),sQuery(id+"F3.wireOp",EDGE,"E18"),sQuery(id+"F3.wireOp",EDGE,"E19"),sQuery(id+"F3.wireOp",EDGE,"E20"),sQuery(id+"F3.wireOp",EDGE,"E21"),sQuery(id+"F3.wireOp",EDGE,"E22"),sQuery(id+"F3.wireOp",EDGE,"E23"),sQuery(id+"F3.wireOp",EDGE,"E24"),sQuery(id+"F3.wireOp",EDGE,"E25"),sQuery(id+"F3.wireOp",EDGE,"E26"),sQuery(id+"F3.wireOp",EDGE,"E27"),sQuery(id+"F3.wireOp",EDGE,"E28"),sQuery(id+"F3.wireOp",EDGE,"E29"),sQuery(id+"F3.wireOp",EDGE,"E30"),sQuery(id+"F3.wireOp",EDGE,"E31"),sQuery(id+"F3.wireOp",EDGE,"E32"),sQuery(id+"F3.wireOp",EDGE,"E33"),sQuery(id+"F3.wireOp",EDGE,"E34"),sQuery(id+"F3.wireOp",EDGE,"E35"),sQuery(id+"F3.wireOp",EDGE,"E36"),sQuery(id+"F3.wireOp",EDGE,"E37"),sQuery(id+"F3.wireOp",EDGE,"E38"),sQuery(id+"F3.wireOp",EDGE,"E39"),sQuery(id+"F3.wireOp",EDGE,"E40"),sQuery(id+"F3.wireOp",EDGE,"E41"),sQuery(id+"F3.wireOp",EDGE,"E42"),sQuery(id+"F3.wireOp",EDGE,"E43"),sQuery(id+"F3.wireOp",EDGE,"E44"),sQuery(id+"F3.wireOp",EDGE,"E45"),sQuery(id+"F3.wireOp",EDGE,"E46"),sQuery(id+"F3.wireOp",EDGE,"E47"),sQuery(id+"F3.wireOp",EDGE,"E48"),sQuery(id+"F3.wireOp",EDGE,"E49"),sQuery(id+"F3.wireOp",EDGE,"E50"),sQuery(id+"F3.wireOp",EDGE,"E51"),sQuery(id+"F3.wireOp",EDGE,"E52"),sQuery(id+"F3.wireOp",EDGE,"E53"),sQuery(id+"F3.wireOp",EDGE,"E54"),sQuery(id+"F3.wireOp",EDGE,"E55"),sQuery(id+"F3.wireOp",EDGE,"E56"),sQuery(id+"F3.wireOp",EDGE,"E57"),sQuery(id+"F3.wireOp",EDGE,"E58"),sQuery(id+"F3.wireOp",EDGE,"E59"),sQuery(id+"F3.wireOp",EDGE,"E60"),sQuery(id+"F3.wireOp",EDGE,"E61"),sQuery(id+"F3.wireOp",EDGE,"E62"),sQuery(id+"F3.wireOp",EDGE,"E63"),sQuery(id+"F3.wireOp",EDGE,"E64"),sQuery(id+"F3.wireOp",EDGE,"E65"),sQuery(id+"F3.wireOp",EDGE,"E66"),sQuery(id+"F3.wireOp",EDGE,"E67"),sQuery(id+"F3.wireOp",EDGE,"E68"),sQuery(id+"F3.wireOp",EDGE,"E69"),sQuery(id+"F3.wireOp",EDGE,"E70"),sQuery(id+"F3.wireOp",EDGE,"E71"),sQuery(id+"F3.wireOp",EDGE,"E72"),sQuery(id+"F3.wireOp",EDGE,"E73"),sQuery(id+"F3.wireOp",EDGE,"E74"),sQuery(id+"F3.wireOp",EDGE,"E75"),sQuery(id+"F3.wireOp",EDGE,"E76"),sQuery(id+"F3.wireOp",EDGE,"E77"),sQuery(id+"F3.wireOp",EDGE,"E78"),sQuery(id+"F3.wireOp",EDGE,"E79"),sQuery(id+"F3.wireOp",EDGE,"E80"),sQuery(id+"F3.wireOp",EDGE,"E81"),sQuery(id+"F3.wireOp",EDGE,"E82"),sQuery(id+"F3.wireOp",EDGE,"E83"),sQuery(id+"F3.wireOp",EDGE,"E84"),sQuery(id+"F3.wireOp",EDGE,"E85"),sQuery(id+"F3.wireOp",EDGE,"E86"),sQuery(id+"F3.wireOp",EDGE,"E87"),sQuery(id+"F3.wireOp",EDGE,"E88"),sQuery(id+"F3.wireOp",EDGE,"E89"),sQuery(id+"F3.wireOp",EDGE,"E90"),sQuery(id+"F3.wireOp",EDGE,"E91"),sQuery(id+"F3.wireOp",EDGE,"E92"),sQuery(id+"F3.wireOp",EDGE,"E93"),sQuery(id+"F3.wireOp",EDGE,"E94"),sQuery(id+"F3.wireOp",EDGE,"E95"),sQuery(id+"F3.wireOp",EDGE,"E96"),sQuery(id+"F3.wireOp",EDGE,"E97"),sQuery(id+"F3.wireOp",EDGE,"E98"),sQuery(id+"F3.wireOp",EDGE,"E99"),sQuery(id+"F3.wireOp",EDGE,"E100"),sQuery(id+"F3.wireOp",EDGE,"E101"),sQuery(id+"F3.wireOp",EDGE,"E102"),sQuery(id+"F3.wireOp",EDGE,"E103"),sQuery(id+"F3.wireOp",EDGE,"E104"),sQuery(id+"F3.wireOp",EDGE,"E105"),sQuery(id+"F3.wireOp",EDGE,"E106"),sQuery(id+"F3.wireOp",EDGE,"E107"),sQuery(id+"F3.wireOp",EDGE,"E108"),sQuery(id+"F3.wireOp",EDGE,"E109"),sQuery(id+"F3.wireOp",EDGE,"E110"),sQuery(id+"F3.wireOp",EDGE,"E111"),sQuery(id+"F3.wireOp",EDGE,"E112"),sQuery(id+"F3.wireOp",EDGE,"E113"),sQuery(id+"F3.wireOp",EDGE,"E114"),sQuery(id+"F3.wireOp",EDGE,"E115"),sQuery(id+"F3.wireOp",EDGE,"E116"),sQuery(id+"F3.wireOp",EDGE,"E117"),sQuery(id+"F3.wireOp",EDGE,"E118"),sQuery(id+"F3.wireOp",EDGE,"E119"),sQuery(id+"F3.wireOp",EDGE,"E120"),sQuery(id+"F3.wireOp",EDGE,"E121"),sQuery(id+"F3.wireOp",EDGE,"E122"),sQuery(id+"F3.wireOp",EDGE,"E123"),sQuery(id+"F3.wireOp",EDGE,"E124"),sQuery(id+"F3.wireOp",EDGE,"E125"),sQuery(id+"F3.wireOp",EDGE,"E126"),sQuery(id+"F3.wireOp",EDGE,"E127"),sQuery(id+"F3.wireOp",EDGE,"E128"),sQuery(id+"F3.wireOp",EDGE,"E129"),sQuery(id+"F3.wireOp",EDGE,"E130"),sQuery(id+"F3.wireOp",EDGE,"E131"),sQuery(id+"F3.wireOp",EDGE,"E132"),sQuery(id+"F3.wireOp",EDGE,"E133"),sQuery(id+"F3.wireOp",EDGE,"E134"),sQuery(id+"F3.wireOp",EDGE,"E135"),sQuery(id+"F3.wireOp",EDGE,"E136"),sQuery(id+"F3.wireOp",EDGE,"E137"),sQuery(id+"F3.wireOp",EDGE,"E138"),sQuery(id+"F3.wireOp",EDGE,"E139"),sQuery(id+"F3.wireOp",EDGE,"E140"),sQuery(id+"F3.wireOp",EDGE,"E141"),sQuery(id+"F3.wireOp",EDGE,"E142"),sQuery(id+"F3.wireOp",EDGE,"E143"),sQuery(id+"F3.wireOp",EDGE,"E144"),sQuery(id+"F3.wireOp",EDGE,"E145"),sQuery(id+"F3.wireOp",EDGE,"E146"),sQuery(id+"F3.wireOp",EDGE,"E147"),sQuery(id+"F3.wireOp",EDGE,"E148"),sQuery(id+"F3.wireOp",EDGE,"E149"),sQuery(id+"F3.wireOp",EDGE,"E150"),sQuery(id+"F3.wireOp",EDGE,"E151"),sQuery(id+"F3.wireOp",EDGE,"E152"),sQuery(id+"F3.wireOp",EDGE,"E153"),sQuery(id+"F3.wireOp",EDGE,"E154"),sQuery(id+"F3.wireOp",EDGE,"E155"),sQuery(id+"F3.wireOp",EDGE,"E156"),sQuery(id+"F3.wireOp",EDGE,"E157"),sQuery(id+"F3.wireOp",EDGE,"E158"),sQuery(id+"F3.wireOp",EDGE,"E159"),sQuery(id+"F3.wireOp",EDGE,"E160"),sQuery(id+"F3.wireOp",EDGE,"E161"),sQuery(id+"F3.wireOp",EDGE,"E162"),sQuery(id+"F3.wireOp",EDGE,"E163"),sQuery(id+"F3.wireOp",EDGE,"E164"),sQuery(id+"F3.wireOp",EDGE,"E165"),sQuery(id+"F3.wireOp",EDGE,"E166"),sQuery(id+"F3.wireOp",EDGE,"E167"),sQuery(id+"F3.wireOp",EDGE,"E168"),sQuery(id+"F3.wireOp",EDGE,"E169"),sQuery(id+"F3.wireOp",EDGE,"E170"),sQuery(id+"F3.wireOp",EDGE,"E171"),sQuery(id+"F3.wireOp",EDGE,"E172"),sQuery(id+"F3.wireOp",EDGE,"E173")])]});
            var Q1;
            Q1=makeQuery(id+"F6.opExtrude","CAP_EDGE",EDGE,{"disambiguationData":[OSD([sQuery(id+"F5.wireOp",EDGE,"E174")])],"isStart":false});
            var Q2;
            Q2=makeQuery(id+"F6.opExtrude","CAP_EDGE",EDGE,{"disambiguationData":[OSD([sQuery(id+"F5.wireOp",EDGE,"E174")])],"isStart":false});
            transform(context, id + "F11", {"entities" : qUnion([Q0]), "transformType" : TransformType.ROTATION, "transformAxis" : qUnion([Q2]), "angle" : 90 * degree, "oppositeDirection" : true, "makeCopy" : false});
        }
    });
